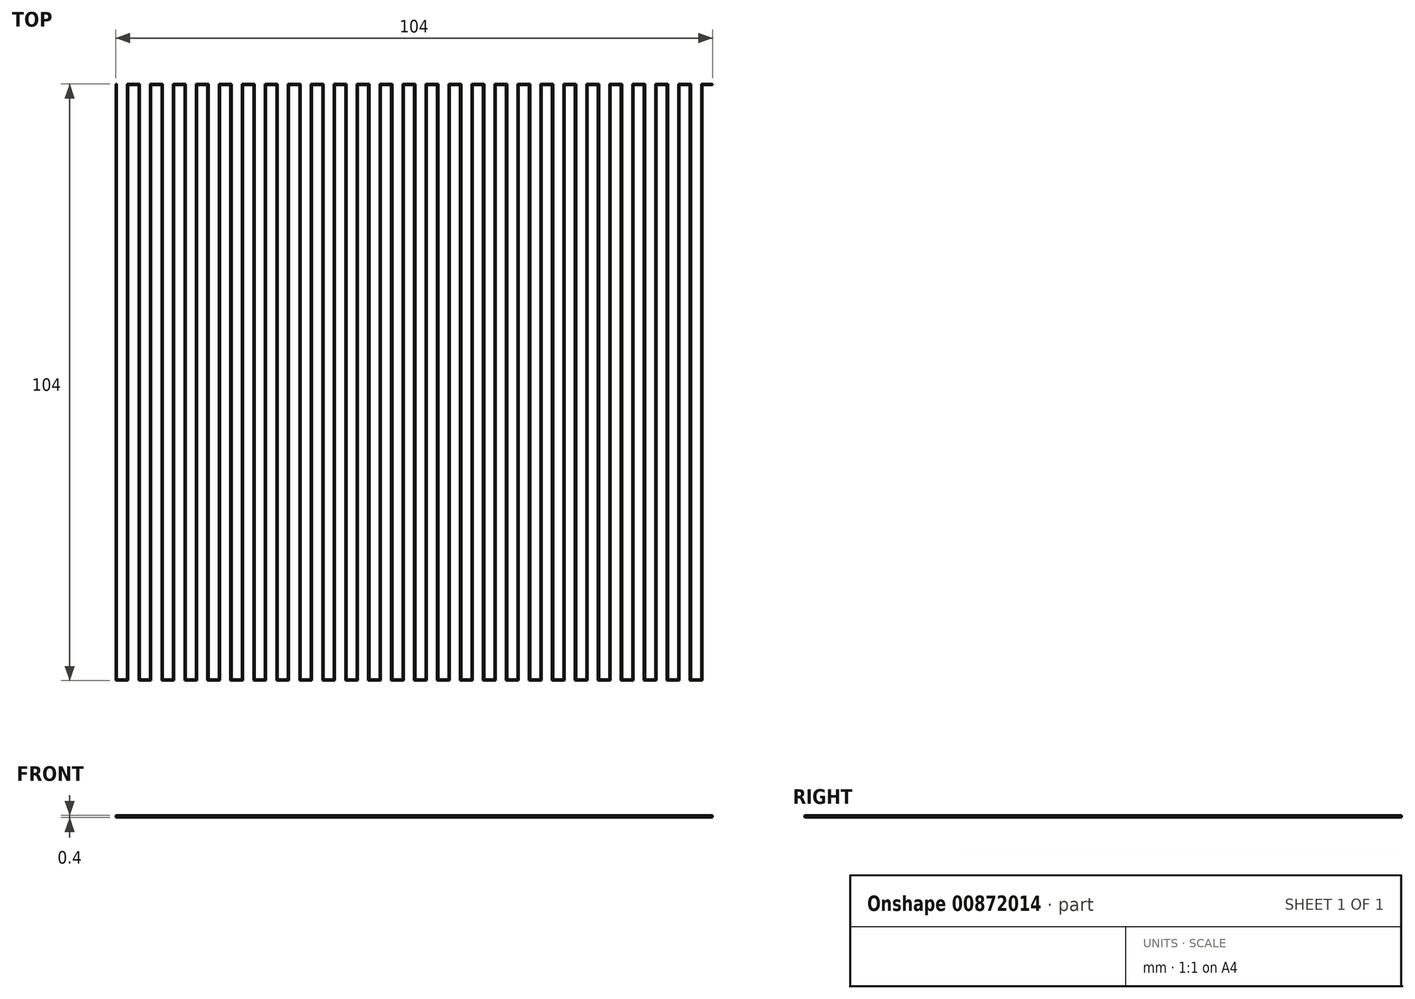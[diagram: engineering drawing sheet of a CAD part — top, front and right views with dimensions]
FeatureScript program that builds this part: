
annotation { "Feature Type Name" : "Feature", "Feature Type Description" : "" }
export const myFeature = defineFeature(function(context is Context, id is Id, definition is map)
    precondition{}
    {
        {
            var Q0;
            Q0=qCreatedBy(makeId("Top.planeOp"),FACE);
            var sketch = newSketch(context, id + "F0", { "sketchPlane" : qUnion([Q0])});
            skLineSegment(sketch, "E0.bottom", {"start": v(-50.6, 46.07) * mm, "end": v(-50.4, 46.07) * mm});
            skLineSegment(sketch, "E0.top", {"start": v(-50.6, -57.93) * mm, "end": v(-50.4, -57.93) * mm});
            skLineSegment(sketch, "E0.left", {"start": v(-50.6, 46.07) * mm, "end": v(-50.6, -57.93) * mm});
            skLineSegment(sketch, "E0.right", {"start": v(-50.4, 46.07) * mm, "end": v(-50.4, -57.93) * mm});
            skLineSegment(sketch, "E1.bottom", {"start": v(-50.6, -57.93) * mm, "end": v(-48.6, -57.93) * mm});
            skLineSegment(sketch, "E1.top", {"start": v(-50.6, -57.73) * mm, "end": v(-48.6, -57.73) * mm});
            skLineSegment(sketch, "E1.left", {"start": v(-50.6, -57.93) * mm, "end": v(-50.6, -57.73) * mm});
            skLineSegment(sketch, "E1.right", {"start": v(-48.6, -57.93) * mm, "end": v(-48.6, -57.73) * mm});
            skLineSegment(sketch, "E2.bottom", {"start": v(-48.6, -57.93) * mm, "end": v(-48.4, -57.93) * mm});
            skLineSegment(sketch, "E2.top", {"start": v(-48.6, 46.07) * mm, "end": v(-48.4, 46.07) * mm});
            skLineSegment(sketch, "E2.left", {"start": v(-48.6, -57.93) * mm, "end": v(-48.6, 46.07) * mm});
            skLineSegment(sketch, "E2.right", {"start": v(-48.4, -57.93) * mm, "end": v(-48.4, 46.07) * mm});
            skLineSegment(sketch, "E3.bottom", {"start": v(-48.6, 46.07) * mm, "end": v(-46.6, 46.07) * mm});
            skLineSegment(sketch, "E3.top", {"start": v(-48.6, 45.87) * mm, "end": v(-46.6, 45.87) * mm});
            skLineSegment(sketch, "E3.left", {"start": v(-48.6, 46.07) * mm, "end": v(-48.6, 45.87) * mm});
            skLineSegment(sketch, "E3.right", {"start": v(-46.6, 46.07) * mm, "end": v(-46.6, 45.87) * mm});
            skLineSegment(sketch, "E4.1.0.0", {"start": v(-46.4, 46.07) * mm, "end": v(-46.4, -57.93) * mm});
            skLineSegment(sketch, "E4.1.0.1", {"start": v(-46.6, 46.07) * mm, "end": v(-46.6, -57.93) * mm});
            skLineSegment(sketch, "E4.1.0.2", {"start": v(-44.4, -57.93) * mm, "end": v(-44.4, 46.07) * mm});
            skLineSegment(sketch, "E4.1.0.3", {"start": v(-44.6, -57.93) * mm, "end": v(-44.6, 46.07) * mm});
            skLineSegment(sketch, "E4.1.0.4", {"start": v(-44.6, 45.87) * mm, "end": v(-42.6, 45.87) * mm});
            skLineSegment(sketch, "E4.1.0.5", {"start": v(-46.6, 46.07) * mm, "end": v(-46.4, 46.07) * mm});
            skLineSegment(sketch, "E4.1.0.6", {"start": v(-44.6, 46.07) * mm, "end": v(-42.6, 46.07) * mm});
            skLineSegment(sketch, "E4.1.0.7", {"start": v(-42.6, 46.07) * mm, "end": v(-42.6, 45.87) * mm});
            skLineSegment(sketch, "E4.1.0.8", {"start": v(-46.6, -57.73) * mm, "end": v(-44.6, -57.73) * mm});
            skLineSegment(sketch, "E4.1.0.9", {"start": v(-46.6, -57.93) * mm, "end": v(-44.6, -57.93) * mm});
            skLineSegment(sketch, "E4.1.0.10", {"start": v(-46.6, -57.93) * mm, "end": v(-46.4, -57.93) * mm});
            skLineSegment(sketch, "E4.1.0.11", {"start": v(-46.6, -57.93) * mm, "end": v(-46.6, -57.73) * mm});
            skLineSegment(sketch, "E4.1.0.12", {"start": v(-44.6, -57.93) * mm, "end": v(-44.6, -57.73) * mm});
            skLineSegment(sketch, "E4.1.0.13", {"start": v(-44.6, -57.93) * mm, "end": v(-44.4, -57.93) * mm});
            skLineSegment(sketch, "E4.1.0.14", {"start": v(-44.6, 46.07) * mm, "end": v(-44.4, 46.07) * mm});
            skLineSegment(sketch, "E4.1.0.15", {"start": v(-44.6, 46.07) * mm, "end": v(-44.6, 45.87) * mm});
            skLineSegment(sketch, "E4.2.0.0", {"start": v(-42.4, 46.07) * mm, "end": v(-42.4, -57.93) * mm});
            skLineSegment(sketch, "E4.2.0.1", {"start": v(-42.6, 46.07) * mm, "end": v(-42.6, -57.93) * mm});
            skLineSegment(sketch, "E4.2.0.2", {"start": v(-40.4, -57.93) * mm, "end": v(-40.4, 46.07) * mm});
            skLineSegment(sketch, "E4.2.0.3", {"start": v(-40.6, -57.93) * mm, "end": v(-40.6, 46.07) * mm});
            skLineSegment(sketch, "E4.2.0.4", {"start": v(-40.6, 45.87) * mm, "end": v(-38.6, 45.87) * mm});
            skLineSegment(sketch, "E4.2.0.5", {"start": v(-42.6, 46.07) * mm, "end": v(-42.4, 46.07) * mm});
            skLineSegment(sketch, "E4.2.0.6", {"start": v(-40.6, 46.07) * mm, "end": v(-38.6, 46.07) * mm});
            skLineSegment(sketch, "E4.2.0.7", {"start": v(-38.6, 46.07) * mm, "end": v(-38.6, 45.87) * mm});
            skLineSegment(sketch, "E4.2.0.8", {"start": v(-42.6, -57.73) * mm, "end": v(-40.6, -57.73) * mm});
            skLineSegment(sketch, "E4.2.0.9", {"start": v(-42.6, -57.93) * mm, "end": v(-40.6, -57.93) * mm});
            skLineSegment(sketch, "E4.2.0.10", {"start": v(-42.6, -57.93) * mm, "end": v(-42.4, -57.93) * mm});
            skLineSegment(sketch, "E4.2.0.11", {"start": v(-42.6, -57.93) * mm, "end": v(-42.6, -57.73) * mm});
            skLineSegment(sketch, "E4.2.0.12", {"start": v(-40.6, -57.93) * mm, "end": v(-40.6, -57.73) * mm});
            skLineSegment(sketch, "E4.2.0.13", {"start": v(-40.6, -57.93) * mm, "end": v(-40.4, -57.93) * mm});
            skLineSegment(sketch, "E4.2.0.14", {"start": v(-40.6, 46.07) * mm, "end": v(-40.4, 46.07) * mm});
            skLineSegment(sketch, "E4.2.0.15", {"start": v(-40.6, 46.07) * mm, "end": v(-40.6, 45.87) * mm});
            skLineSegment(sketch, "E4.3.0.0", {"start": v(-38.4, 46.07) * mm, "end": v(-38.4, -57.93) * mm});
            skLineSegment(sketch, "E4.3.0.1", {"start": v(-38.6, 46.07) * mm, "end": v(-38.6, -57.93) * mm});
            skLineSegment(sketch, "E4.3.0.2", {"start": v(-36.4, -57.93) * mm, "end": v(-36.4, 46.07) * mm});
            skLineSegment(sketch, "E4.3.0.3", {"start": v(-36.6, -57.93) * mm, "end": v(-36.6, 46.07) * mm});
            skLineSegment(sketch, "E4.3.0.4", {"start": v(-36.6, 45.87) * mm, "end": v(-34.6, 45.87) * mm});
            skLineSegment(sketch, "E4.3.0.5", {"start": v(-38.6, 46.07) * mm, "end": v(-38.4, 46.07) * mm});
            skLineSegment(sketch, "E4.3.0.6", {"start": v(-36.6, 46.07) * mm, "end": v(-34.6, 46.07) * mm});
            skLineSegment(sketch, "E4.3.0.7", {"start": v(-34.6, 46.07) * mm, "end": v(-34.6, 45.87) * mm});
            skLineSegment(sketch, "E4.3.0.8", {"start": v(-38.6, -57.73) * mm, "end": v(-36.6, -57.73) * mm});
            skLineSegment(sketch, "E4.3.0.9", {"start": v(-38.6, -57.93) * mm, "end": v(-36.6, -57.93) * mm});
            skLineSegment(sketch, "E4.3.0.10", {"start": v(-38.6, -57.93) * mm, "end": v(-38.4, -57.93) * mm});
            skLineSegment(sketch, "E4.3.0.11", {"start": v(-38.6, -57.93) * mm, "end": v(-38.6, -57.73) * mm});
            skLineSegment(sketch, "E4.3.0.12", {"start": v(-36.6, -57.93) * mm, "end": v(-36.6, -57.73) * mm});
            skLineSegment(sketch, "E4.3.0.13", {"start": v(-36.6, -57.93) * mm, "end": v(-36.4, -57.93) * mm});
            skLineSegment(sketch, "E4.3.0.14", {"start": v(-36.6, 46.07) * mm, "end": v(-36.4, 46.07) * mm});
            skLineSegment(sketch, "E4.3.0.15", {"start": v(-36.6, 46.07) * mm, "end": v(-36.6, 45.87) * mm});
            skLineSegment(sketch, "E4.4.0.0", {"start": v(-34.4, 46.07) * mm, "end": v(-34.4, -57.93) * mm});
            skLineSegment(sketch, "E4.4.0.1", {"start": v(-34.6, 46.07) * mm, "end": v(-34.6, -57.93) * mm});
            skLineSegment(sketch, "E4.4.0.2", {"start": v(-32.4, -57.93) * mm, "end": v(-32.4, 46.07) * mm});
            skLineSegment(sketch, "E4.4.0.3", {"start": v(-32.6, -57.93) * mm, "end": v(-32.6, 46.07) * mm});
            skLineSegment(sketch, "E4.4.0.4", {"start": v(-32.6, 45.87) * mm, "end": v(-30.6, 45.87) * mm});
            skLineSegment(sketch, "E4.4.0.5", {"start": v(-34.6, 46.07) * mm, "end": v(-34.4, 46.07) * mm});
            skLineSegment(sketch, "E4.4.0.6", {"start": v(-32.6, 46.07) * mm, "end": v(-30.6, 46.07) * mm});
            skLineSegment(sketch, "E4.4.0.7", {"start": v(-30.6, 46.07) * mm, "end": v(-30.6, 45.87) * mm});
            skLineSegment(sketch, "E4.4.0.8", {"start": v(-34.6, -57.73) * mm, "end": v(-32.6, -57.73) * mm});
            skLineSegment(sketch, "E4.4.0.9", {"start": v(-34.6, -57.93) * mm, "end": v(-32.6, -57.93) * mm});
            skLineSegment(sketch, "E4.4.0.10", {"start": v(-34.6, -57.93) * mm, "end": v(-34.4, -57.93) * mm});
            skLineSegment(sketch, "E4.4.0.11", {"start": v(-34.6, -57.93) * mm, "end": v(-34.6, -57.73) * mm});
            skLineSegment(sketch, "E4.4.0.12", {"start": v(-32.6, -57.93) * mm, "end": v(-32.6, -57.73) * mm});
            skLineSegment(sketch, "E4.4.0.13", {"start": v(-32.6, -57.93) * mm, "end": v(-32.4, -57.93) * mm});
            skLineSegment(sketch, "E4.4.0.14", {"start": v(-32.6, 46.07) * mm, "end": v(-32.4, 46.07) * mm});
            skLineSegment(sketch, "E4.4.0.15", {"start": v(-32.6, 46.07) * mm, "end": v(-32.6, 45.87) * mm});
            skLineSegment(sketch, "E4.5.0.0", {"start": v(-30.4, 46.07) * mm, "end": v(-30.4, -57.93) * mm});
            skLineSegment(sketch, "E4.5.0.1", {"start": v(-30.6, 46.07) * mm, "end": v(-30.6, -57.93) * mm});
            skLineSegment(sketch, "E4.5.0.2", {"start": v(-28.4, -57.93) * mm, "end": v(-28.4, 46.07) * mm});
            skLineSegment(sketch, "E4.5.0.3", {"start": v(-28.6, -57.93) * mm, "end": v(-28.6, 46.07) * mm});
            skLineSegment(sketch, "E4.5.0.4", {"start": v(-28.6, 45.87) * mm, "end": v(-26.6, 45.87) * mm});
            skLineSegment(sketch, "E4.5.0.5", {"start": v(-30.6, 46.07) * mm, "end": v(-30.4, 46.07) * mm});
            skLineSegment(sketch, "E4.5.0.6", {"start": v(-28.6, 46.07) * mm, "end": v(-26.6, 46.07) * mm});
            skLineSegment(sketch, "E4.5.0.7", {"start": v(-26.6, 46.07) * mm, "end": v(-26.6, 45.87) * mm});
            skLineSegment(sketch, "E4.5.0.8", {"start": v(-30.6, -57.73) * mm, "end": v(-28.6, -57.73) * mm});
            skLineSegment(sketch, "E4.5.0.9", {"start": v(-30.6, -57.93) * mm, "end": v(-28.6, -57.93) * mm});
            skLineSegment(sketch, "E4.5.0.10", {"start": v(-30.6, -57.93) * mm, "end": v(-30.4, -57.93) * mm});
            skLineSegment(sketch, "E4.5.0.11", {"start": v(-30.6, -57.93) * mm, "end": v(-30.6, -57.73) * mm});
            skLineSegment(sketch, "E4.5.0.12", {"start": v(-28.6, -57.93) * mm, "end": v(-28.6, -57.73) * mm});
            skLineSegment(sketch, "E4.5.0.13", {"start": v(-28.6, -57.93) * mm, "end": v(-28.4, -57.93) * mm});
            skLineSegment(sketch, "E4.5.0.14", {"start": v(-28.6, 46.07) * mm, "end": v(-28.4, 46.07) * mm});
            skLineSegment(sketch, "E4.5.0.15", {"start": v(-28.6, 46.07) * mm, "end": v(-28.6, 45.87) * mm});
            skLineSegment(sketch, "E4.6.0.0", {"start": v(-26.4, 46.07) * mm, "end": v(-26.4, -57.93) * mm});
            skLineSegment(sketch, "E4.6.0.1", {"start": v(-26.6, 46.07) * mm, "end": v(-26.6, -57.93) * mm});
            skLineSegment(sketch, "E4.6.0.2", {"start": v(-24.4, -57.93) * mm, "end": v(-24.4, 46.07) * mm});
            skLineSegment(sketch, "E4.6.0.3", {"start": v(-24.6, -57.93) * mm, "end": v(-24.6, 46.07) * mm});
            skLineSegment(sketch, "E4.6.0.4", {"start": v(-24.6, 45.87) * mm, "end": v(-22.6, 45.87) * mm});
            skLineSegment(sketch, "E4.6.0.5", {"start": v(-26.6, 46.07) * mm, "end": v(-26.4, 46.07) * mm});
            skLineSegment(sketch, "E4.6.0.6", {"start": v(-24.6, 46.07) * mm, "end": v(-22.6, 46.07) * mm});
            skLineSegment(sketch, "E4.6.0.7", {"start": v(-22.6, 46.07) * mm, "end": v(-22.6, 45.87) * mm});
            skLineSegment(sketch, "E4.6.0.8", {"start": v(-26.6, -57.73) * mm, "end": v(-24.6, -57.73) * mm});
            skLineSegment(sketch, "E4.6.0.9", {"start": v(-26.6, -57.93) * mm, "end": v(-24.6, -57.93) * mm});
            skLineSegment(sketch, "E4.6.0.10", {"start": v(-26.6, -57.93) * mm, "end": v(-26.4, -57.93) * mm});
            skLineSegment(sketch, "E4.6.0.11", {"start": v(-26.6, -57.93) * mm, "end": v(-26.6, -57.73) * mm});
            skLineSegment(sketch, "E4.6.0.12", {"start": v(-24.6, -57.93) * mm, "end": v(-24.6, -57.73) * mm});
            skLineSegment(sketch, "E4.6.0.13", {"start": v(-24.6, -57.93) * mm, "end": v(-24.4, -57.93) * mm});
            skLineSegment(sketch, "E4.6.0.14", {"start": v(-24.6, 46.07) * mm, "end": v(-24.4, 46.07) * mm});
            skLineSegment(sketch, "E4.6.0.15", {"start": v(-24.6, 46.07) * mm, "end": v(-24.6, 45.87) * mm});
            skLineSegment(sketch, "E4.7.0.0", {"start": v(-22.4, 46.07) * mm, "end": v(-22.4, -57.93) * mm});
            skLineSegment(sketch, "E4.7.0.1", {"start": v(-22.6, 46.07) * mm, "end": v(-22.6, -57.93) * mm});
            skLineSegment(sketch, "E4.7.0.2", {"start": v(-20.4, -57.93) * mm, "end": v(-20.4, 46.07) * mm});
            skLineSegment(sketch, "E4.7.0.3", {"start": v(-20.6, -57.93) * mm, "end": v(-20.6, 46.07) * mm});
            skLineSegment(sketch, "E4.7.0.4", {"start": v(-20.6, 45.87) * mm, "end": v(-18.6, 45.87) * mm});
            skLineSegment(sketch, "E4.7.0.5", {"start": v(-22.6, 46.07) * mm, "end": v(-22.4, 46.07) * mm});
            skLineSegment(sketch, "E4.7.0.6", {"start": v(-20.6, 46.07) * mm, "end": v(-18.6, 46.07) * mm});
            skLineSegment(sketch, "E4.7.0.7", {"start": v(-18.6, 46.07) * mm, "end": v(-18.6, 45.87) * mm});
            skLineSegment(sketch, "E4.7.0.8", {"start": v(-22.6, -57.73) * mm, "end": v(-20.6, -57.73) * mm});
            skLineSegment(sketch, "E4.7.0.9", {"start": v(-22.6, -57.93) * mm, "end": v(-20.6, -57.93) * mm});
            skLineSegment(sketch, "E4.7.0.10", {"start": v(-22.6, -57.93) * mm, "end": v(-22.4, -57.93) * mm});
            skLineSegment(sketch, "E4.7.0.11", {"start": v(-22.6, -57.93) * mm, "end": v(-22.6, -57.73) * mm});
            skLineSegment(sketch, "E4.7.0.12", {"start": v(-20.6, -57.93) * mm, "end": v(-20.6, -57.73) * mm});
            skLineSegment(sketch, "E4.7.0.13", {"start": v(-20.6, -57.93) * mm, "end": v(-20.4, -57.93) * mm});
            skLineSegment(sketch, "E4.7.0.14", {"start": v(-20.6, 46.07) * mm, "end": v(-20.4, 46.07) * mm});
            skLineSegment(sketch, "E4.7.0.15", {"start": v(-20.6, 46.07) * mm, "end": v(-20.6, 45.87) * mm});
            skLineSegment(sketch, "E4.8.0.0", {"start": v(-18.4, 46.07) * mm, "end": v(-18.4, -57.93) * mm});
            skLineSegment(sketch, "E4.8.0.1", {"start": v(-18.6, 46.07) * mm, "end": v(-18.6, -57.93) * mm});
            skLineSegment(sketch, "E4.8.0.2", {"start": v(-16.4, -57.93) * mm, "end": v(-16.4, 46.07) * mm});
            skLineSegment(sketch, "E4.8.0.3", {"start": v(-16.6, -57.93) * mm, "end": v(-16.6, 46.07) * mm});
            skLineSegment(sketch, "E4.8.0.4", {"start": v(-16.6, 45.87) * mm, "end": v(-14.6, 45.87) * mm});
            skLineSegment(sketch, "E4.8.0.5", {"start": v(-18.6, 46.07) * mm, "end": v(-18.4, 46.07) * mm});
            skLineSegment(sketch, "E4.8.0.6", {"start": v(-16.6, 46.07) * mm, "end": v(-14.6, 46.07) * mm});
            skLineSegment(sketch, "E4.8.0.7", {"start": v(-14.6, 46.07) * mm, "end": v(-14.6, 45.87) * mm});
            skLineSegment(sketch, "E4.8.0.8", {"start": v(-18.6, -57.73) * mm, "end": v(-16.6, -57.73) * mm});
            skLineSegment(sketch, "E4.8.0.9", {"start": v(-18.6, -57.93) * mm, "end": v(-16.6, -57.93) * mm});
            skLineSegment(sketch, "E4.8.0.10", {"start": v(-18.6, -57.93) * mm, "end": v(-18.4, -57.93) * mm});
            skLineSegment(sketch, "E4.8.0.11", {"start": v(-18.6, -57.93) * mm, "end": v(-18.6, -57.73) * mm});
            skLineSegment(sketch, "E4.8.0.12", {"start": v(-16.6, -57.93) * mm, "end": v(-16.6, -57.73) * mm});
            skLineSegment(sketch, "E4.8.0.13", {"start": v(-16.6, -57.93) * mm, "end": v(-16.4, -57.93) * mm});
            skLineSegment(sketch, "E4.8.0.14", {"start": v(-16.6, 46.07) * mm, "end": v(-16.4, 46.07) * mm});
            skLineSegment(sketch, "E4.8.0.15", {"start": v(-16.6, 46.07) * mm, "end": v(-16.6, 45.87) * mm});
            skLineSegment(sketch, "E4.9.0.0", {"start": v(-14.4, 46.07) * mm, "end": v(-14.4, -57.93) * mm});
            skLineSegment(sketch, "E4.9.0.1", {"start": v(-14.6, 46.07) * mm, "end": v(-14.6, -57.93) * mm});
            skLineSegment(sketch, "E4.9.0.2", {"start": v(-12.4, -57.93) * mm, "end": v(-12.4, 46.07) * mm});
            skLineSegment(sketch, "E4.9.0.3", {"start": v(-12.6, -57.93) * mm, "end": v(-12.6, 46.07) * mm});
            skLineSegment(sketch, "E4.9.0.4", {"start": v(-12.6, 45.87) * mm, "end": v(-10.6, 45.87) * mm});
            skLineSegment(sketch, "E4.9.0.5", {"start": v(-14.6, 46.07) * mm, "end": v(-14.4, 46.07) * mm});
            skLineSegment(sketch, "E4.9.0.6", {"start": v(-12.6, 46.07) * mm, "end": v(-10.6, 46.07) * mm});
            skLineSegment(sketch, "E4.9.0.7", {"start": v(-10.6, 46.07) * mm, "end": v(-10.6, 45.87) * mm});
            skLineSegment(sketch, "E4.9.0.8", {"start": v(-14.6, -57.73) * mm, "end": v(-12.6, -57.73) * mm});
            skLineSegment(sketch, "E4.9.0.9", {"start": v(-14.6, -57.93) * mm, "end": v(-12.6, -57.93) * mm});
            skLineSegment(sketch, "E4.9.0.10", {"start": v(-14.6, -57.93) * mm, "end": v(-14.4, -57.93) * mm});
            skLineSegment(sketch, "E4.9.0.11", {"start": v(-14.6, -57.93) * mm, "end": v(-14.6, -57.73) * mm});
            skLineSegment(sketch, "E4.9.0.12", {"start": v(-12.6, -57.93) * mm, "end": v(-12.6, -57.73) * mm});
            skLineSegment(sketch, "E4.9.0.13", {"start": v(-12.6, -57.93) * mm, "end": v(-12.4, -57.93) * mm});
            skLineSegment(sketch, "E4.9.0.14", {"start": v(-12.6, 46.07) * mm, "end": v(-12.4, 46.07) * mm});
            skLineSegment(sketch, "E4.9.0.15", {"start": v(-12.6, 46.07) * mm, "end": v(-12.6, 45.87) * mm});
            skLineSegment(sketch, "E4.10.0.0", {"start": v(-10.4, 46.07) * mm, "end": v(-10.4, -57.93) * mm});
            skLineSegment(sketch, "E4.10.0.1", {"start": v(-10.6, 46.07) * mm, "end": v(-10.6, -57.93) * mm});
            skLineSegment(sketch, "E4.10.0.2", {"start": v(-8.4, -57.93) * mm, "end": v(-8.4, 46.07) * mm});
            skLineSegment(sketch, "E4.10.0.3", {"start": v(-8.6, -57.93) * mm, "end": v(-8.6, 46.07) * mm});
            skLineSegment(sketch, "E4.10.0.4", {"start": v(-8.6, 45.87) * mm, "end": v(-6.6, 45.87) * mm});
            skLineSegment(sketch, "E4.10.0.5", {"start": v(-10.6, 46.07) * mm, "end": v(-10.4, 46.07) * mm});
            skLineSegment(sketch, "E4.10.0.6", {"start": v(-8.6, 46.07) * mm, "end": v(-6.6, 46.07) * mm});
            skLineSegment(sketch, "E4.10.0.7", {"start": v(-6.6, 46.07) * mm, "end": v(-6.6, 45.87) * mm});
            skLineSegment(sketch, "E4.10.0.8", {"start": v(-10.6, -57.73) * mm, "end": v(-8.6, -57.73) * mm});
            skLineSegment(sketch, "E4.10.0.9", {"start": v(-10.6, -57.93) * mm, "end": v(-8.6, -57.93) * mm});
            skLineSegment(sketch, "E4.10.0.10", {"start": v(-10.6, -57.93) * mm, "end": v(-10.4, -57.93) * mm});
            skLineSegment(sketch, "E4.10.0.11", {"start": v(-10.6, -57.93) * mm, "end": v(-10.6, -57.73) * mm});
            skLineSegment(sketch, "E4.10.0.12", {"start": v(-8.6, -57.93) * mm, "end": v(-8.6, -57.73) * mm});
            skLineSegment(sketch, "E4.10.0.13", {"start": v(-8.6, -57.93) * mm, "end": v(-8.4, -57.93) * mm});
            skLineSegment(sketch, "E4.10.0.14", {"start": v(-8.6, 46.07) * mm, "end": v(-8.4, 46.07) * mm});
            skLineSegment(sketch, "E4.10.0.15", {"start": v(-8.6, 46.07) * mm, "end": v(-8.6, 45.87) * mm});
            skLineSegment(sketch, "E4.11.0.0", {"start": v(-6.4, 46.07) * mm, "end": v(-6.4, -57.93) * mm});
            skLineSegment(sketch, "E4.11.0.1", {"start": v(-6.6, 46.07) * mm, "end": v(-6.6, -57.93) * mm});
            skLineSegment(sketch, "E4.11.0.2", {"start": v(-4.4, -57.93) * mm, "end": v(-4.4, 46.07) * mm});
            skLineSegment(sketch, "E4.11.0.3", {"start": v(-4.6, -57.93) * mm, "end": v(-4.6, 46.07) * mm});
            skLineSegment(sketch, "E4.11.0.4", {"start": v(-4.6, 45.87) * mm, "end": v(-2.6, 45.87) * mm});
            skLineSegment(sketch, "E4.11.0.5", {"start": v(-6.6, 46.07) * mm, "end": v(-6.4, 46.07) * mm});
            skLineSegment(sketch, "E4.11.0.6", {"start": v(-4.6, 46.07) * mm, "end": v(-2.6, 46.07) * mm});
            skLineSegment(sketch, "E4.11.0.7", {"start": v(-2.6, 46.07) * mm, "end": v(-2.6, 45.87) * mm});
            skLineSegment(sketch, "E4.11.0.8", {"start": v(-6.6, -57.73) * mm, "end": v(-4.6, -57.73) * mm});
            skLineSegment(sketch, "E4.11.0.9", {"start": v(-6.6, -57.93) * mm, "end": v(-4.6, -57.93) * mm});
            skLineSegment(sketch, "E4.11.0.10", {"start": v(-6.6, -57.93) * mm, "end": v(-6.4, -57.93) * mm});
            skLineSegment(sketch, "E4.11.0.11", {"start": v(-6.6, -57.93) * mm, "end": v(-6.6, -57.73) * mm});
            skLineSegment(sketch, "E4.11.0.12", {"start": v(-4.6, -57.93) * mm, "end": v(-4.6, -57.73) * mm});
            skLineSegment(sketch, "E4.11.0.13", {"start": v(-4.6, -57.93) * mm, "end": v(-4.4, -57.93) * mm});
            skLineSegment(sketch, "E4.11.0.14", {"start": v(-4.6, 46.07) * mm, "end": v(-4.4, 46.07) * mm});
            skLineSegment(sketch, "E4.11.0.15", {"start": v(-4.6, 46.07) * mm, "end": v(-4.6, 45.87) * mm});
            skLineSegment(sketch, "E4.12.0.0", {"start": v(-2.4, 46.07) * mm, "end": v(-2.4, -57.93) * mm});
            skLineSegment(sketch, "E4.12.0.1", {"start": v(-2.6, 46.07) * mm, "end": v(-2.6, -57.93) * mm});
            skLineSegment(sketch, "E4.12.0.2", {"start": v(-0.4, -57.93) * mm, "end": v(-0.4, 46.07) * mm});
            skLineSegment(sketch, "E4.12.0.3", {"start": v(-0.6, -57.93) * mm, "end": v(-0.6, 46.07) * mm});
            skLineSegment(sketch, "E4.12.0.4", {"start": v(-0.6, 45.87) * mm, "end": v(1.4, 45.87) * mm});
            skLineSegment(sketch, "E4.12.0.5", {"start": v(-2.6, 46.07) * mm, "end": v(-2.4, 46.07) * mm});
            skLineSegment(sketch, "E4.12.0.6", {"start": v(-0.6, 46.07) * mm, "end": v(1.4, 46.07) * mm});
            skLineSegment(sketch, "E4.12.0.7", {"start": v(1.4, 46.07) * mm, "end": v(1.4, 45.87) * mm});
            skLineSegment(sketch, "E4.12.0.8", {"start": v(-2.6, -57.73) * mm, "end": v(-0.6, -57.73) * mm});
            skLineSegment(sketch, "E4.12.0.9", {"start": v(-2.6, -57.93) * mm, "end": v(-0.6, -57.93) * mm});
            skLineSegment(sketch, "E4.12.0.10", {"start": v(-2.6, -57.93) * mm, "end": v(-2.4, -57.93) * mm});
            skLineSegment(sketch, "E4.12.0.11", {"start": v(-2.6, -57.93) * mm, "end": v(-2.6, -57.73) * mm});
            skLineSegment(sketch, "E4.12.0.12", {"start": v(-0.6, -57.93) * mm, "end": v(-0.6, -57.73) * mm});
            skLineSegment(sketch, "E4.12.0.13", {"start": v(-0.6, -57.93) * mm, "end": v(-0.4, -57.93) * mm});
            skLineSegment(sketch, "E4.12.0.14", {"start": v(-0.6, 46.07) * mm, "end": v(-0.4, 46.07) * mm});
            skLineSegment(sketch, "E4.12.0.15", {"start": v(-0.6, 46.07) * mm, "end": v(-0.6, 45.87) * mm});
            skLineSegment(sketch, "E4.13.0.0", {"start": v(1.6, 46.07) * mm, "end": v(1.6, -57.93) * mm});
            skLineSegment(sketch, "E4.13.0.1", {"start": v(1.4, 46.07) * mm, "end": v(1.4, -57.93) * mm});
            skLineSegment(sketch, "E4.13.0.2", {"start": v(3.6, -57.93) * mm, "end": v(3.6, 46.07) * mm});
            skLineSegment(sketch, "E4.13.0.3", {"start": v(3.4, -57.93) * mm, "end": v(3.4, 46.07) * mm});
            skLineSegment(sketch, "E4.13.0.4", {"start": v(3.4, 45.87) * mm, "end": v(5.4, 45.87) * mm});
            skLineSegment(sketch, "E4.13.0.5", {"start": v(1.4, 46.07) * mm, "end": v(1.6, 46.07) * mm});
            skLineSegment(sketch, "E4.13.0.6", {"start": v(3.4, 46.07) * mm, "end": v(5.4, 46.07) * mm});
            skLineSegment(sketch, "E4.13.0.7", {"start": v(5.4, 46.07) * mm, "end": v(5.4, 45.87) * mm});
            skLineSegment(sketch, "E4.13.0.8", {"start": v(1.4, -57.73) * mm, "end": v(3.4, -57.73) * mm});
            skLineSegment(sketch, "E4.13.0.9", {"start": v(1.4, -57.93) * mm, "end": v(3.4, -57.93) * mm});
            skLineSegment(sketch, "E4.13.0.10", {"start": v(1.4, -57.93) * mm, "end": v(1.6, -57.93) * mm});
            skLineSegment(sketch, "E4.13.0.11", {"start": v(1.4, -57.93) * mm, "end": v(1.4, -57.73) * mm});
            skLineSegment(sketch, "E4.13.0.12", {"start": v(3.4, -57.93) * mm, "end": v(3.4, -57.73) * mm});
            skLineSegment(sketch, "E4.13.0.13", {"start": v(3.4, -57.93) * mm, "end": v(3.6, -57.93) * mm});
            skLineSegment(sketch, "E4.13.0.14", {"start": v(3.4, 46.07) * mm, "end": v(3.6, 46.07) * mm});
            skLineSegment(sketch, "E4.13.0.15", {"start": v(3.4, 46.07) * mm, "end": v(3.4, 45.87) * mm});
            skLineSegment(sketch, "E4.14.0.0", {"start": v(5.6, 46.07) * mm, "end": v(5.6, -57.93) * mm});
            skLineSegment(sketch, "E4.14.0.1", {"start": v(5.4, 46.07) * mm, "end": v(5.4, -57.93) * mm});
            skLineSegment(sketch, "E4.14.0.2", {"start": v(7.6, -57.93) * mm, "end": v(7.6, 46.07) * mm});
            skLineSegment(sketch, "E4.14.0.3", {"start": v(7.4, -57.93) * mm, "end": v(7.4, 46.07) * mm});
            skLineSegment(sketch, "E4.14.0.4", {"start": v(7.4, 45.87) * mm, "end": v(9.4, 45.87) * mm});
            skLineSegment(sketch, "E4.14.0.5", {"start": v(5.4, 46.07) * mm, "end": v(5.6, 46.07) * mm});
            skLineSegment(sketch, "E4.14.0.6", {"start": v(7.4, 46.07) * mm, "end": v(9.4, 46.07) * mm});
            skLineSegment(sketch, "E4.14.0.7", {"start": v(9.4, 46.07) * mm, "end": v(9.4, 45.87) * mm});
            skLineSegment(sketch, "E4.14.0.8", {"start": v(5.4, -57.73) * mm, "end": v(7.4, -57.73) * mm});
            skLineSegment(sketch, "E4.14.0.9", {"start": v(5.4, -57.93) * mm, "end": v(7.4, -57.93) * mm});
            skLineSegment(sketch, "E4.14.0.10", {"start": v(5.4, -57.93) * mm, "end": v(5.6, -57.93) * mm});
            skLineSegment(sketch, "E4.14.0.11", {"start": v(5.4, -57.93) * mm, "end": v(5.4, -57.73) * mm});
            skLineSegment(sketch, "E4.14.0.12", {"start": v(7.4, -57.93) * mm, "end": v(7.4, -57.73) * mm});
            skLineSegment(sketch, "E4.14.0.13", {"start": v(7.4, -57.93) * mm, "end": v(7.6, -57.93) * mm});
            skLineSegment(sketch, "E4.14.0.14", {"start": v(7.4, 46.07) * mm, "end": v(7.6, 46.07) * mm});
            skLineSegment(sketch, "E4.14.0.15", {"start": v(7.4, 46.07) * mm, "end": v(7.4, 45.87) * mm});
            skLineSegment(sketch, "E4.15.0.0", {"start": v(9.6, 46.07) * mm, "end": v(9.6, -57.93) * mm});
            skLineSegment(sketch, "E4.15.0.1", {"start": v(9.4, 46.07) * mm, "end": v(9.4, -57.93) * mm});
            skLineSegment(sketch, "E4.15.0.2", {"start": v(11.6, -57.93) * mm, "end": v(11.6, 46.07) * mm});
            skLineSegment(sketch, "E4.15.0.3", {"start": v(11.4, -57.93) * mm, "end": v(11.4, 46.07) * mm});
            skLineSegment(sketch, "E4.15.0.4", {"start": v(11.4, 45.87) * mm, "end": v(13.4, 45.87) * mm});
            skLineSegment(sketch, "E4.15.0.5", {"start": v(9.4, 46.07) * mm, "end": v(9.6, 46.07) * mm});
            skLineSegment(sketch, "E4.15.0.6", {"start": v(11.4, 46.07) * mm, "end": v(13.4, 46.07) * mm});
            skLineSegment(sketch, "E4.15.0.7", {"start": v(13.4, 46.07) * mm, "end": v(13.4, 45.87) * mm});
            skLineSegment(sketch, "E4.15.0.8", {"start": v(9.4, -57.73) * mm, "end": v(11.4, -57.73) * mm});
            skLineSegment(sketch, "E4.15.0.9", {"start": v(9.4, -57.93) * mm, "end": v(11.4, -57.93) * mm});
            skLineSegment(sketch, "E4.15.0.10", {"start": v(9.4, -57.93) * mm, "end": v(9.6, -57.93) * mm});
            skLineSegment(sketch, "E4.15.0.11", {"start": v(9.4, -57.93) * mm, "end": v(9.4, -57.73) * mm});
            skLineSegment(sketch, "E4.15.0.12", {"start": v(11.4, -57.93) * mm, "end": v(11.4, -57.73) * mm});
            skLineSegment(sketch, "E4.15.0.13", {"start": v(11.4, -57.93) * mm, "end": v(11.6, -57.93) * mm});
            skLineSegment(sketch, "E4.15.0.14", {"start": v(11.4, 46.07) * mm, "end": v(11.6, 46.07) * mm});
            skLineSegment(sketch, "E4.15.0.15", {"start": v(11.4, 46.07) * mm, "end": v(11.4, 45.87) * mm});
            skLineSegment(sketch, "E4.16.0.0", {"start": v(13.6, 46.07) * mm, "end": v(13.6, -57.93) * mm});
            skLineSegment(sketch, "E4.16.0.1", {"start": v(13.4, 46.07) * mm, "end": v(13.4, -57.93) * mm});
            skLineSegment(sketch, "E4.16.0.2", {"start": v(15.6, -57.93) * mm, "end": v(15.6, 46.07) * mm});
            skLineSegment(sketch, "E4.16.0.3", {"start": v(15.4, -57.93) * mm, "end": v(15.4, 46.07) * mm});
            skLineSegment(sketch, "E4.16.0.4", {"start": v(15.4, 45.87) * mm, "end": v(17.4, 45.87) * mm});
            skLineSegment(sketch, "E4.16.0.5", {"start": v(13.4, 46.07) * mm, "end": v(13.6, 46.07) * mm});
            skLineSegment(sketch, "E4.16.0.6", {"start": v(15.4, 46.07) * mm, "end": v(17.4, 46.07) * mm});
            skLineSegment(sketch, "E4.16.0.7", {"start": v(17.4, 46.07) * mm, "end": v(17.4, 45.87) * mm});
            skLineSegment(sketch, "E4.16.0.8", {"start": v(13.4, -57.73) * mm, "end": v(15.4, -57.73) * mm});
            skLineSegment(sketch, "E4.16.0.9", {"start": v(13.4, -57.93) * mm, "end": v(15.4, -57.93) * mm});
            skLineSegment(sketch, "E4.16.0.10", {"start": v(13.4, -57.93) * mm, "end": v(13.6, -57.93) * mm});
            skLineSegment(sketch, "E4.16.0.11", {"start": v(13.4, -57.93) * mm, "end": v(13.4, -57.73) * mm});
            skLineSegment(sketch, "E4.16.0.12", {"start": v(15.4, -57.93) * mm, "end": v(15.4, -57.73) * mm});
            skLineSegment(sketch, "E4.16.0.13", {"start": v(15.4, -57.93) * mm, "end": v(15.6, -57.93) * mm});
            skLineSegment(sketch, "E4.16.0.14", {"start": v(15.4, 46.07) * mm, "end": v(15.6, 46.07) * mm});
            skLineSegment(sketch, "E4.16.0.15", {"start": v(15.4, 46.07) * mm, "end": v(15.4, 45.87) * mm});
            skLineSegment(sketch, "E4.17.0.0", {"start": v(17.6, 46.07) * mm, "end": v(17.6, -57.93) * mm});
            skLineSegment(sketch, "E4.17.0.1", {"start": v(17.4, 46.07) * mm, "end": v(17.4, -57.93) * mm});
            skLineSegment(sketch, "E4.17.0.2", {"start": v(19.6, -57.93) * mm, "end": v(19.6, 46.07) * mm});
            skLineSegment(sketch, "E4.17.0.3", {"start": v(19.4, -57.93) * mm, "end": v(19.4, 46.07) * mm});
            skLineSegment(sketch, "E4.17.0.4", {"start": v(19.4, 45.87) * mm, "end": v(21.4, 45.87) * mm});
            skLineSegment(sketch, "E4.17.0.5", {"start": v(17.4, 46.07) * mm, "end": v(17.6, 46.07) * mm});
            skLineSegment(sketch, "E4.17.0.6", {"start": v(19.4, 46.07) * mm, "end": v(21.4, 46.07) * mm});
            skLineSegment(sketch, "E4.17.0.7", {"start": v(21.4, 46.07) * mm, "end": v(21.4, 45.87) * mm});
            skLineSegment(sketch, "E4.17.0.8", {"start": v(17.4, -57.73) * mm, "end": v(19.4, -57.73) * mm});
            skLineSegment(sketch, "E4.17.0.9", {"start": v(17.4, -57.93) * mm, "end": v(19.4, -57.93) * mm});
            skLineSegment(sketch, "E4.17.0.10", {"start": v(17.4, -57.93) * mm, "end": v(17.6, -57.93) * mm});
            skLineSegment(sketch, "E4.17.0.11", {"start": v(17.4, -57.93) * mm, "end": v(17.4, -57.73) * mm});
            skLineSegment(sketch, "E4.17.0.12", {"start": v(19.4, -57.93) * mm, "end": v(19.4, -57.73) * mm});
            skLineSegment(sketch, "E4.17.0.13", {"start": v(19.4, -57.93) * mm, "end": v(19.6, -57.93) * mm});
            skLineSegment(sketch, "E4.17.0.14", {"start": v(19.4, 46.07) * mm, "end": v(19.6, 46.07) * mm});
            skLineSegment(sketch, "E4.17.0.15", {"start": v(19.4, 46.07) * mm, "end": v(19.4, 45.87) * mm});
            skLineSegment(sketch, "E4.direction1", {"start": v(-50.6, -57.93) * mm, "end": v(-46.6, -57.93) * mm, "construction": true});
            skLineSegment(sketch, "E5.0.18.0", {"start": v(21.6, 46.07) * mm, "end": v(21.6, -57.93) * mm});
            skLineSegment(sketch, "E5.3.18.0", {"start": v(21.4, 46.07) * mm, "end": v(21.4, -57.93) * mm});
            skLineSegment(sketch, "E5.6.18.0", {"start": v(23.6, -57.93) * mm, "end": v(23.6, 46.07) * mm});
            skLineSegment(sketch, "E5.9.18.0", {"start": v(23.4, -57.93) * mm, "end": v(23.4, 46.07) * mm});
            skLineSegment(sketch, "E5.12.18.0", {"start": v(23.4, 45.87) * mm, "end": v(25.4, 45.87) * mm});
            skLineSegment(sketch, "E5.15.18.0", {"start": v(21.4, 46.07) * mm, "end": v(21.6, 46.07) * mm});
            skLineSegment(sketch, "E5.18.18.0", {"start": v(23.4, 46.07) * mm, "end": v(25.4, 46.07) * mm});
            skLineSegment(sketch, "E5.21.18.0", {"start": v(25.4, 46.07) * mm, "end": v(25.4, 45.87) * mm});
            skLineSegment(sketch, "E5.24.18.0", {"start": v(21.4, -57.73) * mm, "end": v(23.4, -57.73) * mm});
            skLineSegment(sketch, "E5.27.18.0", {"start": v(21.4, -57.93) * mm, "end": v(23.4, -57.93) * mm});
            skLineSegment(sketch, "E5.30.18.0", {"start": v(21.4, -57.93) * mm, "end": v(21.6, -57.93) * mm});
            skLineSegment(sketch, "E5.33.18.0", {"start": v(21.4, -57.93) * mm, "end": v(21.4, -57.73) * mm});
            skLineSegment(sketch, "E5.36.18.0", {"start": v(23.4, -57.93) * mm, "end": v(23.4, -57.73) * mm});
            skLineSegment(sketch, "E5.39.18.0", {"start": v(23.4, -57.93) * mm, "end": v(23.6, -57.93) * mm});
            skLineSegment(sketch, "E5.42.18.0", {"start": v(23.4, 46.07) * mm, "end": v(23.6, 46.07) * mm});
            skLineSegment(sketch, "E5.45.18.0", {"start": v(23.4, 46.07) * mm, "end": v(23.4, 45.87) * mm});
            skLineSegment(sketch, "E5.0.19.0", {"start": v(25.6, 46.07) * mm, "end": v(25.6, -57.93) * mm});
            skLineSegment(sketch, "E5.3.19.0", {"start": v(25.4, 46.07) * mm, "end": v(25.4, -57.93) * mm});
            skLineSegment(sketch, "E5.6.19.0", {"start": v(27.6, -57.93) * mm, "end": v(27.6, 46.07) * mm});
            skLineSegment(sketch, "E5.9.19.0", {"start": v(27.4, -57.93) * mm, "end": v(27.4, 46.07) * mm});
            skLineSegment(sketch, "E5.12.19.0", {"start": v(27.4, 45.87) * mm, "end": v(29.4, 45.87) * mm});
            skLineSegment(sketch, "E5.15.19.0", {"start": v(25.4, 46.07) * mm, "end": v(25.6, 46.07) * mm});
            skLineSegment(sketch, "E5.18.19.0", {"start": v(27.4, 46.07) * mm, "end": v(29.4, 46.07) * mm});
            skLineSegment(sketch, "E5.21.19.0", {"start": v(29.4, 46.07) * mm, "end": v(29.4, 45.87) * mm});
            skLineSegment(sketch, "E5.24.19.0", {"start": v(25.4, -57.73) * mm, "end": v(27.4, -57.73) * mm});
            skLineSegment(sketch, "E5.27.19.0", {"start": v(25.4, -57.93) * mm, "end": v(27.4, -57.93) * mm});
            skLineSegment(sketch, "E5.30.19.0", {"start": v(25.4, -57.93) * mm, "end": v(25.6, -57.93) * mm});
            skLineSegment(sketch, "E5.33.19.0", {"start": v(25.4, -57.93) * mm, "end": v(25.4, -57.73) * mm});
            skLineSegment(sketch, "E5.36.19.0", {"start": v(27.4, -57.93) * mm, "end": v(27.4, -57.73) * mm});
            skLineSegment(sketch, "E5.39.19.0", {"start": v(27.4, -57.93) * mm, "end": v(27.6, -57.93) * mm});
            skLineSegment(sketch, "E5.42.19.0", {"start": v(27.4, 46.07) * mm, "end": v(27.6, 46.07) * mm});
            skLineSegment(sketch, "E5.45.19.0", {"start": v(27.4, 46.07) * mm, "end": v(27.4, 45.87) * mm});
            skLineSegment(sketch, "E5.0.20.0", {"start": v(29.6, 46.07) * mm, "end": v(29.6, -57.93) * mm});
            skLineSegment(sketch, "E5.3.20.0", {"start": v(29.4, 46.07) * mm, "end": v(29.4, -57.93) * mm});
            skLineSegment(sketch, "E5.6.20.0", {"start": v(31.6, -57.93) * mm, "end": v(31.6, 46.07) * mm});
            skLineSegment(sketch, "E5.9.20.0", {"start": v(31.4, -57.93) * mm, "end": v(31.4, 46.07) * mm});
            skLineSegment(sketch, "E5.12.20.0", {"start": v(31.4, 45.87) * mm, "end": v(33.4, 45.87) * mm});
            skLineSegment(sketch, "E5.15.20.0", {"start": v(29.4, 46.07) * mm, "end": v(29.6, 46.07) * mm});
            skLineSegment(sketch, "E5.18.20.0", {"start": v(31.4, 46.07) * mm, "end": v(33.4, 46.07) * mm});
            skLineSegment(sketch, "E5.21.20.0", {"start": v(33.4, 46.07) * mm, "end": v(33.4, 45.87) * mm});
            skLineSegment(sketch, "E5.24.20.0", {"start": v(29.4, -57.73) * mm, "end": v(31.4, -57.73) * mm});
            skLineSegment(sketch, "E5.27.20.0", {"start": v(29.4, -57.93) * mm, "end": v(31.4, -57.93) * mm});
            skLineSegment(sketch, "E5.30.20.0", {"start": v(29.4, -57.93) * mm, "end": v(29.6, -57.93) * mm});
            skLineSegment(sketch, "E5.33.20.0", {"start": v(29.4, -57.93) * mm, "end": v(29.4, -57.73) * mm});
            skLineSegment(sketch, "E5.36.20.0", {"start": v(31.4, -57.93) * mm, "end": v(31.4, -57.73) * mm});
            skLineSegment(sketch, "E5.39.20.0", {"start": v(31.4, -57.93) * mm, "end": v(31.6, -57.93) * mm});
            skLineSegment(sketch, "E5.42.20.0", {"start": v(31.4, 46.07) * mm, "end": v(31.6, 46.07) * mm});
            skLineSegment(sketch, "E5.45.20.0", {"start": v(31.4, 46.07) * mm, "end": v(31.4, 45.87) * mm});
            skLineSegment(sketch, "E5.0.21.0", {"start": v(33.6, 46.07) * mm, "end": v(33.6, -57.93) * mm});
            skLineSegment(sketch, "E5.3.21.0", {"start": v(33.4, 46.07) * mm, "end": v(33.4, -57.93) * mm});
            skLineSegment(sketch, "E5.6.21.0", {"start": v(35.6, -57.93) * mm, "end": v(35.6, 46.07) * mm});
            skLineSegment(sketch, "E5.9.21.0", {"start": v(35.4, -57.93) * mm, "end": v(35.4, 46.07) * mm});
            skLineSegment(sketch, "E5.12.21.0", {"start": v(35.4, 45.87) * mm, "end": v(37.4, 45.87) * mm});
            skLineSegment(sketch, "E5.15.21.0", {"start": v(33.4, 46.07) * mm, "end": v(33.6, 46.07) * mm});
            skLineSegment(sketch, "E5.18.21.0", {"start": v(35.4, 46.07) * mm, "end": v(37.4, 46.07) * mm});
            skLineSegment(sketch, "E5.21.21.0", {"start": v(37.4, 46.07) * mm, "end": v(37.4, 45.87) * mm});
            skLineSegment(sketch, "E5.24.21.0", {"start": v(33.4, -57.73) * mm, "end": v(35.4, -57.73) * mm});
            skLineSegment(sketch, "E5.27.21.0", {"start": v(33.4, -57.93) * mm, "end": v(35.4, -57.93) * mm});
            skLineSegment(sketch, "E5.30.21.0", {"start": v(33.4, -57.93) * mm, "end": v(33.6, -57.93) * mm});
            skLineSegment(sketch, "E5.33.21.0", {"start": v(33.4, -57.93) * mm, "end": v(33.4, -57.73) * mm});
            skLineSegment(sketch, "E5.36.21.0", {"start": v(35.4, -57.93) * mm, "end": v(35.4, -57.73) * mm});
            skLineSegment(sketch, "E5.39.21.0", {"start": v(35.4, -57.93) * mm, "end": v(35.6, -57.93) * mm});
            skLineSegment(sketch, "E5.42.21.0", {"start": v(35.4, 46.07) * mm, "end": v(35.6, 46.07) * mm});
            skLineSegment(sketch, "E5.45.21.0", {"start": v(35.4, 46.07) * mm, "end": v(35.4, 45.87) * mm});
            skLineSegment(sketch, "E5.0.22.0", {"start": v(37.6, 46.07) * mm, "end": v(37.6, -57.93) * mm});
            skLineSegment(sketch, "E5.3.22.0", {"start": v(37.4, 46.07) * mm, "end": v(37.4, -57.93) * mm});
            skLineSegment(sketch, "E5.6.22.0", {"start": v(39.6, -57.93) * mm, "end": v(39.6, 46.07) * mm});
            skLineSegment(sketch, "E5.9.22.0", {"start": v(39.4, -57.93) * mm, "end": v(39.4, 46.07) * mm});
            skLineSegment(sketch, "E5.12.22.0", {"start": v(39.4, 45.87) * mm, "end": v(41.4, 45.87) * mm});
            skLineSegment(sketch, "E5.15.22.0", {"start": v(37.4, 46.07) * mm, "end": v(37.6, 46.07) * mm});
            skLineSegment(sketch, "E5.18.22.0", {"start": v(39.4, 46.07) * mm, "end": v(41.4, 46.07) * mm});
            skLineSegment(sketch, "E5.21.22.0", {"start": v(41.4, 46.07) * mm, "end": v(41.4, 45.87) * mm});
            skLineSegment(sketch, "E5.24.22.0", {"start": v(37.4, -57.73) * mm, "end": v(39.4, -57.73) * mm});
            skLineSegment(sketch, "E5.27.22.0", {"start": v(37.4, -57.93) * mm, "end": v(39.4, -57.93) * mm});
            skLineSegment(sketch, "E5.30.22.0", {"start": v(37.4, -57.93) * mm, "end": v(37.6, -57.93) * mm});
            skLineSegment(sketch, "E5.33.22.0", {"start": v(37.4, -57.93) * mm, "end": v(37.4, -57.73) * mm});
            skLineSegment(sketch, "E5.36.22.0", {"start": v(39.4, -57.93) * mm, "end": v(39.4, -57.73) * mm});
            skLineSegment(sketch, "E5.39.22.0", {"start": v(39.4, -57.93) * mm, "end": v(39.6, -57.93) * mm});
            skLineSegment(sketch, "E5.42.22.0", {"start": v(39.4, 46.07) * mm, "end": v(39.6, 46.07) * mm});
            skLineSegment(sketch, "E5.45.22.0", {"start": v(39.4, 46.07) * mm, "end": v(39.4, 45.87) * mm});
            skLineSegment(sketch, "E5.0.23.0", {"start": v(41.6, 46.07) * mm, "end": v(41.6, -57.93) * mm});
            skLineSegment(sketch, "E5.3.23.0", {"start": v(41.4, 46.07) * mm, "end": v(41.4, -57.93) * mm});
            skLineSegment(sketch, "E5.6.23.0", {"start": v(43.6, -57.93) * mm, "end": v(43.6, 46.07) * mm});
            skLineSegment(sketch, "E5.9.23.0", {"start": v(43.4, -57.93) * mm, "end": v(43.4, 46.07) * mm});
            skLineSegment(sketch, "E5.12.23.0", {"start": v(43.4, 45.87) * mm, "end": v(45.4, 45.87) * mm});
            skLineSegment(sketch, "E5.15.23.0", {"start": v(41.4, 46.07) * mm, "end": v(41.6, 46.07) * mm});
            skLineSegment(sketch, "E5.18.23.0", {"start": v(43.4, 46.07) * mm, "end": v(45.4, 46.07) * mm});
            skLineSegment(sketch, "E5.21.23.0", {"start": v(45.4, 46.07) * mm, "end": v(45.4, 45.87) * mm});
            skLineSegment(sketch, "E5.24.23.0", {"start": v(41.4, -57.73) * mm, "end": v(43.4, -57.73) * mm});
            skLineSegment(sketch, "E5.27.23.0", {"start": v(41.4, -57.93) * mm, "end": v(43.4, -57.93) * mm});
            skLineSegment(sketch, "E5.30.23.0", {"start": v(41.4, -57.93) * mm, "end": v(41.6, -57.93) * mm});
            skLineSegment(sketch, "E5.33.23.0", {"start": v(41.4, -57.93) * mm, "end": v(41.4, -57.73) * mm});
            skLineSegment(sketch, "E5.36.23.0", {"start": v(43.4, -57.93) * mm, "end": v(43.4, -57.73) * mm});
            skLineSegment(sketch, "E5.39.23.0", {"start": v(43.4, -57.93) * mm, "end": v(43.6, -57.93) * mm});
            skLineSegment(sketch, "E5.42.23.0", {"start": v(43.4, 46.07) * mm, "end": v(43.6, 46.07) * mm});
            skLineSegment(sketch, "E5.45.23.0", {"start": v(43.4, 46.07) * mm, "end": v(43.4, 45.87) * mm});
            skLineSegment(sketch, "E5.0.24.0", {"start": v(45.6, 46.07) * mm, "end": v(45.6, -57.93) * mm});
            skLineSegment(sketch, "E5.3.24.0", {"start": v(45.4, 46.07) * mm, "end": v(45.4, -57.93) * mm});
            skLineSegment(sketch, "E5.6.24.0", {"start": v(47.6, -57.93) * mm, "end": v(47.6, 46.07) * mm});
            skLineSegment(sketch, "E5.9.24.0", {"start": v(47.4, -57.93) * mm, "end": v(47.4, 46.07) * mm});
            skLineSegment(sketch, "E5.12.24.0", {"start": v(47.4, 45.87) * mm, "end": v(49.4, 45.87) * mm});
            skLineSegment(sketch, "E5.15.24.0", {"start": v(45.4, 46.07) * mm, "end": v(45.6, 46.07) * mm});
            skLineSegment(sketch, "E5.18.24.0", {"start": v(47.4, 46.07) * mm, "end": v(49.4, 46.07) * mm});
            skLineSegment(sketch, "E5.21.24.0", {"start": v(49.4, 46.07) * mm, "end": v(49.4, 45.87) * mm});
            skLineSegment(sketch, "E5.24.24.0", {"start": v(45.4, -57.73) * mm, "end": v(47.4, -57.73) * mm});
            skLineSegment(sketch, "E5.27.24.0", {"start": v(45.4, -57.93) * mm, "end": v(47.4, -57.93) * mm});
            skLineSegment(sketch, "E5.30.24.0", {"start": v(45.4, -57.93) * mm, "end": v(45.6, -57.93) * mm});
            skLineSegment(sketch, "E5.33.24.0", {"start": v(45.4, -57.93) * mm, "end": v(45.4, -57.73) * mm});
            skLineSegment(sketch, "E5.36.24.0", {"start": v(47.4, -57.93) * mm, "end": v(47.4, -57.73) * mm});
            skLineSegment(sketch, "E5.39.24.0", {"start": v(47.4, -57.93) * mm, "end": v(47.6, -57.93) * mm});
            skLineSegment(sketch, "E5.42.24.0", {"start": v(47.4, 46.07) * mm, "end": v(47.6, 46.07) * mm});
            skLineSegment(sketch, "E5.45.24.0", {"start": v(47.4, 46.07) * mm, "end": v(47.4, 45.87) * mm});
            skLineSegment(sketch, "E5.0.25.0", {"start": v(49.6, 46.07) * mm, "end": v(49.6, -57.93) * mm});
            skLineSegment(sketch, "E5.3.25.0", {"start": v(49.4, 46.07) * mm, "end": v(49.4, -57.93) * mm});
            skLineSegment(sketch, "E5.6.25.0", {"start": v(51.6, -57.93) * mm, "end": v(51.6, 46.07) * mm});
            skLineSegment(sketch, "E5.9.25.0", {"start": v(51.4, -57.93) * mm, "end": v(51.4, 46.07) * mm});
            skLineSegment(sketch, "E5.12.25.0", {"start": v(51.4, 45.87) * mm, "end": v(53.4, 45.87) * mm});
            skLineSegment(sketch, "E5.15.25.0", {"start": v(49.4, 46.07) * mm, "end": v(49.6, 46.07) * mm});
            skLineSegment(sketch, "E5.18.25.0", {"start": v(51.4, 46.07) * mm, "end": v(53.4, 46.07) * mm});
            skLineSegment(sketch, "E5.21.25.0", {"start": v(53.4, 46.07) * mm, "end": v(53.4, 45.87) * mm});
            skLineSegment(sketch, "E5.24.25.0", {"start": v(49.4, -57.73) * mm, "end": v(51.4, -57.73) * mm});
            skLineSegment(sketch, "E5.27.25.0", {"start": v(49.4, -57.93) * mm, "end": v(51.4, -57.93) * mm});
            skLineSegment(sketch, "E5.30.25.0", {"start": v(49.4, -57.93) * mm, "end": v(49.6, -57.93) * mm});
            skLineSegment(sketch, "E5.33.25.0", {"start": v(49.4, -57.93) * mm, "end": v(49.4, -57.73) * mm});
            skLineSegment(sketch, "E5.36.25.0", {"start": v(51.4, -57.93) * mm, "end": v(51.4, -57.73) * mm});
            skLineSegment(sketch, "E5.39.25.0", {"start": v(51.4, -57.93) * mm, "end": v(51.6, -57.93) * mm});
            skLineSegment(sketch, "E5.42.25.0", {"start": v(51.4, 46.07) * mm, "end": v(51.6, 46.07) * mm});
            skLineSegment(sketch, "E5.45.25.0", {"start": v(51.4, 46.07) * mm, "end": v(51.4, 45.87) * mm});
            skSolve(sketch);
        }
        {
            var Q0;
            {var subQ0=sQuery(id+"F0.wireOp",EDGE,"E5.18.25.0");var subQ1=sQuery(id+"F0.wireOp",EDGE,"E5.6.25.0");var subQ2=makeQuery(id+"F0.imprint","INTERSECT",VERTEX,{"derivedFrom":[subQ1,subQ0]});var subQ5=makeQuery(id+"F0.imprint","IMPRINT",EDGE,{"disambiguationData":[TD([[subQ2,1.0]])],"derivedFrom":subQ1});var subQ12=sQuery(id+"F0.wireOp",EDGE,"E5.39.25.0");var subQ13=sQuery(id+"F0.wireOp",EDGE,"E5.27.25.0");var subQ16=sQuery(id+"F0.wireOp",EDGE,"E5.0.25.0");var subQ17=makeQuery(id+"F0.imprint","INTERSECT",VERTEX,{"derivedFrom":[subQ16,subQ13]});var subQ19=makeQuery(id+"F0.imprint","IMPRINT",EDGE,{"disambiguationData":[TD([[subQ17,1.0]])],"derivedFrom":subQ16});var subQ25=sQuery(id+"F0.wireOp",EDGE,"E5.21.24.0");var subQ28=makeQuery(id+"F0.imprint","IMPRINT",EDGE,{"derivedFrom":subQ25});var subQ29=sQuery(id+"F0.wireOp",EDGE,"E5.18.24.0");var subQ30=sQuery(id+"F0.wireOp",EDGE,"E5.6.24.0");var subQ31=makeQuery(id+"F0.imprint","INTERSECT",VERTEX,{"derivedFrom":[subQ30,subQ29]});var subQ33=makeQuery(id+"F0.imprint","IMPRINT",EDGE,{"disambiguationData":[TD([[subQ31,1.0]])],"derivedFrom":subQ30});var subQ40=sQuery(id+"F0.wireOp",EDGE,"E5.39.24.0");var subQ41=sQuery(id+"F0.wireOp",EDGE,"E5.27.24.0");var subQ44=sQuery(id+"F0.wireOp",EDGE,"E5.0.24.0");var subQ45=makeQuery(id+"F0.imprint","INTERSECT",VERTEX,{"derivedFrom":[subQ44,subQ41]});var subQ47=makeQuery(id+"F0.imprint","IMPRINT",EDGE,{"disambiguationData":[TD([[subQ45,1.0]])],"derivedFrom":subQ44});var subQ53=sQuery(id+"F0.wireOp",EDGE,"E5.21.23.0");var subQ56=makeQuery(id+"F0.imprint","IMPRINT",EDGE,{"derivedFrom":subQ53});var subQ57=sQuery(id+"F0.wireOp",EDGE,"E5.18.23.0");var subQ58=sQuery(id+"F0.wireOp",EDGE,"E5.6.23.0");var subQ59=makeQuery(id+"F0.imprint","INTERSECT",VERTEX,{"derivedFrom":[subQ58,subQ57]});var subQ61=makeQuery(id+"F0.imprint","IMPRINT",EDGE,{"disambiguationData":[TD([[subQ59,1.0]])],"derivedFrom":subQ58});var subQ68=sQuery(id+"F0.wireOp",EDGE,"E5.39.23.0");var subQ69=sQuery(id+"F0.wireOp",EDGE,"E5.27.23.0");var subQ72=sQuery(id+"F0.wireOp",EDGE,"E5.0.23.0");var subQ73=makeQuery(id+"F0.imprint","INTERSECT",VERTEX,{"derivedFrom":[subQ72,subQ69]});var subQ75=makeQuery(id+"F0.imprint","IMPRINT",EDGE,{"disambiguationData":[TD([[subQ73,1.0]])],"derivedFrom":subQ72});var subQ81=sQuery(id+"F0.wireOp",EDGE,"E5.21.22.0");var subQ84=makeQuery(id+"F0.imprint","IMPRINT",EDGE,{"derivedFrom":subQ81});var subQ85=sQuery(id+"F0.wireOp",EDGE,"E5.18.22.0");var subQ86=sQuery(id+"F0.wireOp",EDGE,"E5.6.22.0");var subQ87=makeQuery(id+"F0.imprint","INTERSECT",VERTEX,{"derivedFrom":[subQ86,subQ85]});var subQ89=makeQuery(id+"F0.imprint","IMPRINT",EDGE,{"disambiguationData":[TD([[subQ87,1.0]])],"derivedFrom":subQ86});var subQ96=sQuery(id+"F0.wireOp",EDGE,"E5.39.22.0");var subQ97=sQuery(id+"F0.wireOp",EDGE,"E5.27.22.0");var subQ100=sQuery(id+"F0.wireOp",EDGE,"E5.0.22.0");var subQ101=makeQuery(id+"F0.imprint","INTERSECT",VERTEX,{"derivedFrom":[subQ100,subQ97]});var subQ103=makeQuery(id+"F0.imprint","IMPRINT",EDGE,{"disambiguationData":[TD([[subQ101,1.0]])],"derivedFrom":subQ100});var subQ109=sQuery(id+"F0.wireOp",EDGE,"E5.21.21.0");var subQ112=makeQuery(id+"F0.imprint","IMPRINT",EDGE,{"derivedFrom":subQ109});var subQ113=sQuery(id+"F0.wireOp",EDGE,"E5.18.21.0");var subQ114=sQuery(id+"F0.wireOp",EDGE,"E5.6.21.0");var subQ115=makeQuery(id+"F0.imprint","INTERSECT",VERTEX,{"derivedFrom":[subQ114,subQ113]});var subQ117=makeQuery(id+"F0.imprint","IMPRINT",EDGE,{"disambiguationData":[TD([[subQ115,1.0]])],"derivedFrom":subQ114});var subQ124=sQuery(id+"F0.wireOp",EDGE,"E5.39.21.0");var subQ125=sQuery(id+"F0.wireOp",EDGE,"E5.27.21.0");var subQ128=sQuery(id+"F0.wireOp",EDGE,"E5.0.21.0");var subQ129=makeQuery(id+"F0.imprint","INTERSECT",VERTEX,{"derivedFrom":[subQ128,subQ125]});var subQ131=makeQuery(id+"F0.imprint","IMPRINT",EDGE,{"disambiguationData":[TD([[subQ129,1.0]])],"derivedFrom":subQ128});var subQ137=sQuery(id+"F0.wireOp",EDGE,"E5.21.20.0");var subQ140=makeQuery(id+"F0.imprint","IMPRINT",EDGE,{"derivedFrom":subQ137});var subQ141=sQuery(id+"F0.wireOp",EDGE,"E5.18.20.0");var subQ142=sQuery(id+"F0.wireOp",EDGE,"E5.6.20.0");var subQ143=makeQuery(id+"F0.imprint","INTERSECT",VERTEX,{"derivedFrom":[subQ142,subQ141]});var subQ145=makeQuery(id+"F0.imprint","IMPRINT",EDGE,{"disambiguationData":[TD([[subQ143,1.0]])],"derivedFrom":subQ142});var subQ152=sQuery(id+"F0.wireOp",EDGE,"E5.39.20.0");var subQ153=sQuery(id+"F0.wireOp",EDGE,"E5.27.20.0");var subQ156=sQuery(id+"F0.wireOp",EDGE,"E5.0.20.0");var subQ157=makeQuery(id+"F0.imprint","INTERSECT",VERTEX,{"derivedFrom":[subQ156,subQ153]});var subQ159=makeQuery(id+"F0.imprint","IMPRINT",EDGE,{"disambiguationData":[TD([[subQ157,1.0]])],"derivedFrom":subQ156});var subQ165=sQuery(id+"F0.wireOp",EDGE,"E5.21.19.0");var subQ168=makeQuery(id+"F0.imprint","IMPRINT",EDGE,{"derivedFrom":subQ165});var subQ169=sQuery(id+"F0.wireOp",EDGE,"E5.18.19.0");var subQ170=sQuery(id+"F0.wireOp",EDGE,"E5.6.19.0");var subQ171=makeQuery(id+"F0.imprint","INTERSECT",VERTEX,{"derivedFrom":[subQ170,subQ169]});var subQ173=makeQuery(id+"F0.imprint","IMPRINT",EDGE,{"disambiguationData":[TD([[subQ171,1.0]])],"derivedFrom":subQ170});var subQ180=sQuery(id+"F0.wireOp",EDGE,"E5.39.19.0");var subQ181=sQuery(id+"F0.wireOp",EDGE,"E5.27.19.0");var subQ184=sQuery(id+"F0.wireOp",EDGE,"E5.0.19.0");var subQ185=makeQuery(id+"F0.imprint","INTERSECT",VERTEX,{"derivedFrom":[subQ184,subQ181]});var subQ187=makeQuery(id+"F0.imprint","IMPRINT",EDGE,{"disambiguationData":[TD([[subQ185,1.0]])],"derivedFrom":subQ184});var subQ193=sQuery(id+"F0.wireOp",EDGE,"E5.21.18.0");var subQ196=makeQuery(id+"F0.imprint","IMPRINT",EDGE,{"derivedFrom":subQ193});var subQ197=sQuery(id+"F0.wireOp",EDGE,"E5.18.18.0");var subQ198=sQuery(id+"F0.wireOp",EDGE,"E5.6.18.0");var subQ199=makeQuery(id+"F0.imprint","INTERSECT",VERTEX,{"derivedFrom":[subQ198,subQ197]});var subQ201=makeQuery(id+"F0.imprint","IMPRINT",EDGE,{"disambiguationData":[TD([[subQ199,1.0]])],"derivedFrom":subQ198});var subQ208=sQuery(id+"F0.wireOp",EDGE,"E5.39.18.0");var subQ209=sQuery(id+"F0.wireOp",EDGE,"E5.27.18.0");var subQ212=sQuery(id+"F0.wireOp",EDGE,"E5.0.18.0");var subQ213=makeQuery(id+"F0.imprint","INTERSECT",VERTEX,{"derivedFrom":[subQ212,subQ209]});var subQ215=makeQuery(id+"F0.imprint","IMPRINT",EDGE,{"disambiguationData":[TD([[subQ213,1.0]])],"derivedFrom":subQ212});var subQ221=sQuery(id+"F0.wireOp",EDGE,"E4.17.0.7");var subQ224=makeQuery(id+"F0.imprint","IMPRINT",EDGE,{"derivedFrom":subQ221});var subQ225=sQuery(id+"F0.wireOp",EDGE,"E4.17.0.6");var subQ226=sQuery(id+"F0.wireOp",EDGE,"E4.17.0.2");var subQ227=makeQuery(id+"F0.imprint","INTERSECT",VERTEX,{"derivedFrom":[subQ226,subQ225]});var subQ229=makeQuery(id+"F0.imprint","IMPRINT",EDGE,{"disambiguationData":[TD([[subQ227,1.0]])],"derivedFrom":subQ226});var subQ236=sQuery(id+"F0.wireOp",EDGE,"E4.17.0.13");var subQ237=sQuery(id+"F0.wireOp",EDGE,"E4.17.0.9");var subQ240=sQuery(id+"F0.wireOp",EDGE,"E4.17.0.0");var subQ241=makeQuery(id+"F0.imprint","INTERSECT",VERTEX,{"derivedFrom":[subQ240,subQ237]});var subQ243=makeQuery(id+"F0.imprint","IMPRINT",EDGE,{"disambiguationData":[TD([[subQ241,1.0]])],"derivedFrom":subQ240});var subQ249=sQuery(id+"F0.wireOp",EDGE,"E4.16.0.7");var subQ252=makeQuery(id+"F0.imprint","IMPRINT",EDGE,{"derivedFrom":subQ249});var subQ253=sQuery(id+"F0.wireOp",EDGE,"E4.16.0.6");var subQ254=sQuery(id+"F0.wireOp",EDGE,"E4.16.0.2");var subQ255=makeQuery(id+"F0.imprint","INTERSECT",VERTEX,{"derivedFrom":[subQ254,subQ253]});var subQ257=makeQuery(id+"F0.imprint","IMPRINT",EDGE,{"disambiguationData":[TD([[subQ255,1.0]])],"derivedFrom":subQ254});var subQ264=sQuery(id+"F0.wireOp",EDGE,"E4.16.0.13");var subQ265=sQuery(id+"F0.wireOp",EDGE,"E4.16.0.9");var subQ268=sQuery(id+"F0.wireOp",EDGE,"E4.16.0.0");var subQ269=makeQuery(id+"F0.imprint","INTERSECT",VERTEX,{"derivedFrom":[subQ268,subQ265]});var subQ271=makeQuery(id+"F0.imprint","IMPRINT",EDGE,{"disambiguationData":[TD([[subQ269,1.0]])],"derivedFrom":subQ268});var subQ277=sQuery(id+"F0.wireOp",EDGE,"E4.15.0.7");var subQ280=makeQuery(id+"F0.imprint","IMPRINT",EDGE,{"derivedFrom":subQ277});var subQ281=sQuery(id+"F0.wireOp",EDGE,"E4.15.0.6");var subQ282=sQuery(id+"F0.wireOp",EDGE,"E4.15.0.2");var subQ283=makeQuery(id+"F0.imprint","INTERSECT",VERTEX,{"derivedFrom":[subQ282,subQ281]});var subQ285=makeQuery(id+"F0.imprint","IMPRINT",EDGE,{"disambiguationData":[TD([[subQ283,1.0]])],"derivedFrom":subQ282});var subQ292=sQuery(id+"F0.wireOp",EDGE,"E4.15.0.13");var subQ293=sQuery(id+"F0.wireOp",EDGE,"E4.15.0.9");var subQ296=sQuery(id+"F0.wireOp",EDGE,"E4.15.0.0");var subQ297=makeQuery(id+"F0.imprint","INTERSECT",VERTEX,{"derivedFrom":[subQ296,subQ293]});var subQ299=makeQuery(id+"F0.imprint","IMPRINT",EDGE,{"disambiguationData":[TD([[subQ297,1.0]])],"derivedFrom":subQ296});var subQ305=sQuery(id+"F0.wireOp",EDGE,"E4.14.0.7");var subQ308=makeQuery(id+"F0.imprint","IMPRINT",EDGE,{"derivedFrom":subQ305});var subQ309=sQuery(id+"F0.wireOp",EDGE,"E4.14.0.6");var subQ310=sQuery(id+"F0.wireOp",EDGE,"E4.14.0.2");var subQ311=makeQuery(id+"F0.imprint","INTERSECT",VERTEX,{"derivedFrom":[subQ310,subQ309]});var subQ313=makeQuery(id+"F0.imprint","IMPRINT",EDGE,{"disambiguationData":[TD([[subQ311,1.0]])],"derivedFrom":subQ310});var subQ320=sQuery(id+"F0.wireOp",EDGE,"E4.14.0.13");var subQ321=sQuery(id+"F0.wireOp",EDGE,"E4.14.0.9");var subQ324=sQuery(id+"F0.wireOp",EDGE,"E4.14.0.0");var subQ325=makeQuery(id+"F0.imprint","INTERSECT",VERTEX,{"derivedFrom":[subQ324,subQ321]});var subQ327=makeQuery(id+"F0.imprint","IMPRINT",EDGE,{"disambiguationData":[TD([[subQ325,1.0]])],"derivedFrom":subQ324});var subQ333=sQuery(id+"F0.wireOp",EDGE,"E4.13.0.7");var subQ336=makeQuery(id+"F0.imprint","IMPRINT",EDGE,{"derivedFrom":subQ333});var subQ337=sQuery(id+"F0.wireOp",EDGE,"E4.13.0.6");var subQ338=sQuery(id+"F0.wireOp",EDGE,"E4.13.0.2");var subQ339=makeQuery(id+"F0.imprint","INTERSECT",VERTEX,{"derivedFrom":[subQ338,subQ337]});var subQ341=makeQuery(id+"F0.imprint","IMPRINT",EDGE,{"disambiguationData":[TD([[subQ339,1.0]])],"derivedFrom":subQ338});var subQ348=sQuery(id+"F0.wireOp",EDGE,"E4.13.0.13");var subQ349=sQuery(id+"F0.wireOp",EDGE,"E4.13.0.9");var subQ352=sQuery(id+"F0.wireOp",EDGE,"E4.13.0.0");var subQ353=makeQuery(id+"F0.imprint","INTERSECT",VERTEX,{"derivedFrom":[subQ352,subQ349]});var subQ355=makeQuery(id+"F0.imprint","IMPRINT",EDGE,{"disambiguationData":[TD([[subQ353,1.0]])],"derivedFrom":subQ352});var subQ361=sQuery(id+"F0.wireOp",EDGE,"E4.12.0.7");var subQ364=makeQuery(id+"F0.imprint","IMPRINT",EDGE,{"derivedFrom":subQ361});var subQ365=sQuery(id+"F0.wireOp",EDGE,"E4.12.0.6");var subQ366=sQuery(id+"F0.wireOp",EDGE,"E4.12.0.2");var subQ367=makeQuery(id+"F0.imprint","INTERSECT",VERTEX,{"derivedFrom":[subQ366,subQ365]});var subQ369=makeQuery(id+"F0.imprint","IMPRINT",EDGE,{"disambiguationData":[TD([[subQ367,1.0]])],"derivedFrom":subQ366});var subQ376=sQuery(id+"F0.wireOp",EDGE,"E4.12.0.13");var subQ377=sQuery(id+"F0.wireOp",EDGE,"E4.12.0.9");var subQ380=sQuery(id+"F0.wireOp",EDGE,"E4.12.0.0");var subQ381=makeQuery(id+"F0.imprint","INTERSECT",VERTEX,{"derivedFrom":[subQ380,subQ377]});var subQ383=makeQuery(id+"F0.imprint","IMPRINT",EDGE,{"disambiguationData":[TD([[subQ381,1.0]])],"derivedFrom":subQ380});var subQ389=sQuery(id+"F0.wireOp",EDGE,"E4.11.0.7");var subQ392=makeQuery(id+"F0.imprint","IMPRINT",EDGE,{"derivedFrom":subQ389});var subQ393=sQuery(id+"F0.wireOp",EDGE,"E4.11.0.6");var subQ394=sQuery(id+"F0.wireOp",EDGE,"E4.11.0.2");var subQ395=makeQuery(id+"F0.imprint","INTERSECT",VERTEX,{"derivedFrom":[subQ394,subQ393]});var subQ397=makeQuery(id+"F0.imprint","IMPRINT",EDGE,{"disambiguationData":[TD([[subQ395,1.0]])],"derivedFrom":subQ394});var subQ404=sQuery(id+"F0.wireOp",EDGE,"E4.11.0.13");var subQ405=sQuery(id+"F0.wireOp",EDGE,"E4.11.0.9");var subQ408=sQuery(id+"F0.wireOp",EDGE,"E4.11.0.0");var subQ409=makeQuery(id+"F0.imprint","INTERSECT",VERTEX,{"derivedFrom":[subQ408,subQ405]});var subQ411=makeQuery(id+"F0.imprint","IMPRINT",EDGE,{"disambiguationData":[TD([[subQ409,1.0]])],"derivedFrom":subQ408});var subQ417=sQuery(id+"F0.wireOp",EDGE,"E4.10.0.7");var subQ420=makeQuery(id+"F0.imprint","IMPRINT",EDGE,{"derivedFrom":subQ417});var subQ421=sQuery(id+"F0.wireOp",EDGE,"E4.10.0.6");var subQ422=sQuery(id+"F0.wireOp",EDGE,"E4.10.0.2");var subQ423=makeQuery(id+"F0.imprint","INTERSECT",VERTEX,{"derivedFrom":[subQ422,subQ421]});var subQ425=makeQuery(id+"F0.imprint","IMPRINT",EDGE,{"disambiguationData":[TD([[subQ423,1.0]])],"derivedFrom":subQ422});var subQ432=sQuery(id+"F0.wireOp",EDGE,"E4.10.0.13");var subQ433=sQuery(id+"F0.wireOp",EDGE,"E4.10.0.9");var subQ436=sQuery(id+"F0.wireOp",EDGE,"E4.10.0.0");var subQ437=makeQuery(id+"F0.imprint","INTERSECT",VERTEX,{"derivedFrom":[subQ436,subQ433]});var subQ439=makeQuery(id+"F0.imprint","IMPRINT",EDGE,{"disambiguationData":[TD([[subQ437,1.0]])],"derivedFrom":subQ436});var subQ445=sQuery(id+"F0.wireOp",EDGE,"E4.9.0.7");var subQ448=makeQuery(id+"F0.imprint","IMPRINT",EDGE,{"derivedFrom":subQ445});var subQ449=sQuery(id+"F0.wireOp",EDGE,"E4.9.0.6");var subQ450=sQuery(id+"F0.wireOp",EDGE,"E4.9.0.2");var subQ451=makeQuery(id+"F0.imprint","INTERSECT",VERTEX,{"derivedFrom":[subQ450,subQ449]});var subQ453=makeQuery(id+"F0.imprint","IMPRINT",EDGE,{"disambiguationData":[TD([[subQ451,1.0]])],"derivedFrom":subQ450});var subQ460=sQuery(id+"F0.wireOp",EDGE,"E4.9.0.13");var subQ461=sQuery(id+"F0.wireOp",EDGE,"E4.9.0.9");var subQ464=sQuery(id+"F0.wireOp",EDGE,"E4.9.0.0");var subQ465=makeQuery(id+"F0.imprint","INTERSECT",VERTEX,{"derivedFrom":[subQ464,subQ461]});var subQ467=makeQuery(id+"F0.imprint","IMPRINT",EDGE,{"disambiguationData":[TD([[subQ465,1.0]])],"derivedFrom":subQ464});var subQ473=sQuery(id+"F0.wireOp",EDGE,"E4.8.0.7");var subQ476=makeQuery(id+"F0.imprint","IMPRINT",EDGE,{"derivedFrom":subQ473});var subQ477=sQuery(id+"F0.wireOp",EDGE,"E4.8.0.6");var subQ478=sQuery(id+"F0.wireOp",EDGE,"E4.8.0.2");var subQ479=makeQuery(id+"F0.imprint","INTERSECT",VERTEX,{"derivedFrom":[subQ478,subQ477]});var subQ481=makeQuery(id+"F0.imprint","IMPRINT",EDGE,{"disambiguationData":[TD([[subQ479,1.0]])],"derivedFrom":subQ478});var subQ488=sQuery(id+"F0.wireOp",EDGE,"E4.8.0.13");var subQ489=sQuery(id+"F0.wireOp",EDGE,"E4.8.0.9");var subQ492=sQuery(id+"F0.wireOp",EDGE,"E4.8.0.0");var subQ493=makeQuery(id+"F0.imprint","INTERSECT",VERTEX,{"derivedFrom":[subQ492,subQ489]});var subQ495=makeQuery(id+"F0.imprint","IMPRINT",EDGE,{"disambiguationData":[TD([[subQ493,1.0]])],"derivedFrom":subQ492});var subQ501=sQuery(id+"F0.wireOp",EDGE,"E4.7.0.7");var subQ504=makeQuery(id+"F0.imprint","IMPRINT",EDGE,{"derivedFrom":subQ501});var subQ505=sQuery(id+"F0.wireOp",EDGE,"E4.7.0.6");var subQ506=sQuery(id+"F0.wireOp",EDGE,"E4.7.0.2");var subQ507=makeQuery(id+"F0.imprint","INTERSECT",VERTEX,{"derivedFrom":[subQ506,subQ505]});var subQ509=makeQuery(id+"F0.imprint","IMPRINT",EDGE,{"disambiguationData":[TD([[subQ507,1.0]])],"derivedFrom":subQ506});var subQ516=sQuery(id+"F0.wireOp",EDGE,"E4.7.0.13");var subQ517=sQuery(id+"F0.wireOp",EDGE,"E4.7.0.9");var subQ520=sQuery(id+"F0.wireOp",EDGE,"E4.7.0.0");var subQ521=makeQuery(id+"F0.imprint","INTERSECT",VERTEX,{"derivedFrom":[subQ520,subQ517]});var subQ523=makeQuery(id+"F0.imprint","IMPRINT",EDGE,{"disambiguationData":[TD([[subQ521,1.0]])],"derivedFrom":subQ520});var subQ529=sQuery(id+"F0.wireOp",EDGE,"E4.6.0.7");var subQ532=makeQuery(id+"F0.imprint","IMPRINT",EDGE,{"derivedFrom":subQ529});var subQ533=sQuery(id+"F0.wireOp",EDGE,"E4.6.0.6");var subQ534=sQuery(id+"F0.wireOp",EDGE,"E4.6.0.2");var subQ535=makeQuery(id+"F0.imprint","INTERSECT",VERTEX,{"derivedFrom":[subQ534,subQ533]});var subQ537=makeQuery(id+"F0.imprint","IMPRINT",EDGE,{"disambiguationData":[TD([[subQ535,1.0]])],"derivedFrom":subQ534});var subQ544=sQuery(id+"F0.wireOp",EDGE,"E4.6.0.13");var subQ545=sQuery(id+"F0.wireOp",EDGE,"E4.6.0.9");var subQ548=sQuery(id+"F0.wireOp",EDGE,"E4.6.0.0");var subQ549=makeQuery(id+"F0.imprint","INTERSECT",VERTEX,{"derivedFrom":[subQ548,subQ545]});var subQ551=makeQuery(id+"F0.imprint","IMPRINT",EDGE,{"disambiguationData":[TD([[subQ549,1.0]])],"derivedFrom":subQ548});var subQ557=sQuery(id+"F0.wireOp",EDGE,"E4.5.0.7");var subQ560=makeQuery(id+"F0.imprint","IMPRINT",EDGE,{"derivedFrom":subQ557});var subQ561=sQuery(id+"F0.wireOp",EDGE,"E4.5.0.6");var subQ562=sQuery(id+"F0.wireOp",EDGE,"E4.5.0.2");var subQ563=makeQuery(id+"F0.imprint","INTERSECT",VERTEX,{"derivedFrom":[subQ562,subQ561]});var subQ565=makeQuery(id+"F0.imprint","IMPRINT",EDGE,{"disambiguationData":[TD([[subQ563,1.0]])],"derivedFrom":subQ562});var subQ572=sQuery(id+"F0.wireOp",EDGE,"E4.5.0.13");var subQ573=sQuery(id+"F0.wireOp",EDGE,"E4.5.0.9");var subQ576=sQuery(id+"F0.wireOp",EDGE,"E4.5.0.0");var subQ577=makeQuery(id+"F0.imprint","INTERSECT",VERTEX,{"derivedFrom":[subQ576,subQ573]});var subQ579=makeQuery(id+"F0.imprint","IMPRINT",EDGE,{"disambiguationData":[TD([[subQ577,1.0]])],"derivedFrom":subQ576});var subQ585=sQuery(id+"F0.wireOp",EDGE,"E4.4.0.7");var subQ588=makeQuery(id+"F0.imprint","IMPRINT",EDGE,{"derivedFrom":subQ585});var subQ589=sQuery(id+"F0.wireOp",EDGE,"E4.4.0.6");var subQ590=sQuery(id+"F0.wireOp",EDGE,"E4.4.0.2");var subQ591=makeQuery(id+"F0.imprint","INTERSECT",VERTEX,{"derivedFrom":[subQ590,subQ589]});var subQ593=makeQuery(id+"F0.imprint","IMPRINT",EDGE,{"disambiguationData":[TD([[subQ591,1.0]])],"derivedFrom":subQ590});var subQ600=sQuery(id+"F0.wireOp",EDGE,"E4.4.0.13");var subQ601=sQuery(id+"F0.wireOp",EDGE,"E4.4.0.9");var subQ604=sQuery(id+"F0.wireOp",EDGE,"E4.4.0.0");var subQ605=makeQuery(id+"F0.imprint","INTERSECT",VERTEX,{"derivedFrom":[subQ604,subQ601]});var subQ607=makeQuery(id+"F0.imprint","IMPRINT",EDGE,{"disambiguationData":[TD([[subQ605,1.0]])],"derivedFrom":subQ604});var subQ613=sQuery(id+"F0.wireOp",EDGE,"E4.3.0.7");var subQ616=makeQuery(id+"F0.imprint","IMPRINT",EDGE,{"derivedFrom":subQ613});var subQ617=sQuery(id+"F0.wireOp",EDGE,"E4.3.0.6");var subQ618=sQuery(id+"F0.wireOp",EDGE,"E4.3.0.2");var subQ619=makeQuery(id+"F0.imprint","INTERSECT",VERTEX,{"derivedFrom":[subQ618,subQ617]});var subQ621=makeQuery(id+"F0.imprint","IMPRINT",EDGE,{"disambiguationData":[TD([[subQ619,1.0]])],"derivedFrom":subQ618});var subQ628=sQuery(id+"F0.wireOp",EDGE,"E4.3.0.13");var subQ629=sQuery(id+"F0.wireOp",EDGE,"E4.3.0.9");var subQ632=sQuery(id+"F0.wireOp",EDGE,"E4.3.0.0");var subQ633=makeQuery(id+"F0.imprint","INTERSECT",VERTEX,{"derivedFrom":[subQ632,subQ629]});var subQ635=makeQuery(id+"F0.imprint","IMPRINT",EDGE,{"disambiguationData":[TD([[subQ633,1.0]])],"derivedFrom":subQ632});var subQ641=sQuery(id+"F0.wireOp",EDGE,"E4.2.0.7");var subQ644=makeQuery(id+"F0.imprint","IMPRINT",EDGE,{"derivedFrom":subQ641});var subQ645=sQuery(id+"F0.wireOp",EDGE,"E4.2.0.6");var subQ646=sQuery(id+"F0.wireOp",EDGE,"E4.2.0.2");var subQ647=makeQuery(id+"F0.imprint","INTERSECT",VERTEX,{"derivedFrom":[subQ646,subQ645]});var subQ649=makeQuery(id+"F0.imprint","IMPRINT",EDGE,{"disambiguationData":[TD([[subQ647,1.0]])],"derivedFrom":subQ646});var subQ656=sQuery(id+"F0.wireOp",EDGE,"E4.2.0.13");var subQ657=sQuery(id+"F0.wireOp",EDGE,"E4.2.0.9");var subQ660=sQuery(id+"F0.wireOp",EDGE,"E4.2.0.0");var subQ661=makeQuery(id+"F0.imprint","INTERSECT",VERTEX,{"derivedFrom":[subQ660,subQ657]});var subQ663=makeQuery(id+"F0.imprint","IMPRINT",EDGE,{"disambiguationData":[TD([[subQ661,1.0]])],"derivedFrom":subQ660});var subQ669=sQuery(id+"F0.wireOp",EDGE,"E4.1.0.7");var subQ672=makeQuery(id+"F0.imprint","IMPRINT",EDGE,{"derivedFrom":subQ669});var subQ673=sQuery(id+"F0.wireOp",EDGE,"E4.1.0.6");var subQ674=sQuery(id+"F0.wireOp",EDGE,"E4.1.0.2");var subQ675=makeQuery(id+"F0.imprint","INTERSECT",VERTEX,{"derivedFrom":[subQ674,subQ673]});var subQ677=makeQuery(id+"F0.imprint","IMPRINT",EDGE,{"disambiguationData":[TD([[subQ675,1.0]])],"derivedFrom":subQ674});var subQ684=sQuery(id+"F0.wireOp",EDGE,"E4.1.0.13");var subQ685=sQuery(id+"F0.wireOp",EDGE,"E4.1.0.9");var subQ688=sQuery(id+"F0.wireOp",EDGE,"E4.1.0.0");var subQ689=makeQuery(id+"F0.imprint","INTERSECT",VERTEX,{"derivedFrom":[subQ688,subQ685]});var subQ691=makeQuery(id+"F0.imprint","IMPRINT",EDGE,{"disambiguationData":[TD([[subQ689,1.0]])],"derivedFrom":subQ688});var subQ697=sQuery(id+"F0.wireOp",EDGE,"E3.right");var subQ700=makeQuery(id+"F0.imprint","IMPRINT",EDGE,{"derivedFrom":subQ697});var subQ701=sQuery(id+"F0.wireOp",EDGE,"E3.bottom");var subQ703=sQuery(id+"F0.wireOp",EDGE,"E2.top");var subQ709=sQuery(id+"F0.wireOp",EDGE,"E1.right");var subQ713=makeQuery(id+"F0.imprint","IMPRINT",EDGE,{"derivedFrom":subQ709});var subQ714=sQuery(id+"F0.wireOp",EDGE,"E1.bottom");var subQ716=sQuery(id+"F0.wireOp",EDGE,"E0.top");var subQ722=sQuery(id+"F0.wireOp",EDGE,"E5.21.25.0");var subQ723=sQuery(id+"F0.wireOp",EDGE,"E0.bottom");Q0=qUnion([makeQuery(id+"F0.imprint","IMPRINT",FACE,{"disambiguationData":[TD([[makeQuery(id+"F0.imprint","IMPRINT",EDGE,{"derivedFrom":subQ723}),-1.0]])]}),makeQuery(id+"F0.imprint","IMPRINT",FACE,{"disambiguationData":[TD([[makeQuery(id+"F0.imprint","IMPRINT",EDGE,{"derivedFrom":subQ722}),-1.0]])]}),makeQuery(id+"F0.imprint","IMPRINT",FACE,{"disambiguationData":[TD([[makeQuery(id+"F0.imprint","IMPRINT",EDGE,{"derivedFrom":subQ716}),1.0]])]}),makeQuery(id+"F0.imprint","IMPRINT",FACE,{"disambiguationData":[TD([[makeQuery(id+"F0.imprint","IMPRINT",EDGE,{"derivedFrom":subQ714}),1.0]])]}),makeQuery(id+"F0.imprint","IMPRINT",FACE,{"disambiguationData":[TD([[subQ713,-1.0]])]}),makeQuery(id+"F0.imprint","IMPRINT",FACE,{"disambiguationData":[TD([[makeQuery(id+"F0.imprint","IMPRINT",EDGE,{"derivedFrom":subQ703}),-1.0]])]}),makeQuery(id+"F0.imprint","IMPRINT",FACE,{"disambiguationData":[TD([[makeQuery(id+"F0.imprint","IMPRINT",EDGE,{"derivedFrom":subQ701}),-1.0]])]}),makeQuery(id+"F0.imprint","IMPRINT",FACE,{"disambiguationData":[TD([[subQ700,1.0]])]}),makeQuery(id+"F0.imprint","IMPRINT",FACE,{"disambiguationData":[TD([[subQ691,-1.0]])]}),makeQuery(id+"F0.imprint","IMPRINT",FACE,{"disambiguationData":[TD([[subQ691,1.0]])]}),makeQuery(id+"F0.imprint","IMPRINT",FACE,{"disambiguationData":[TD([[makeQuery(id+"F0.imprint","IMPRINT",EDGE,{"derivedFrom":subQ684}),1.0]])]}),makeQuery(id+"F0.imprint","IMPRINT",FACE,{"disambiguationData":[TD([[subQ677,1.0]])]}),makeQuery(id+"F0.imprint","IMPRINT",FACE,{"disambiguationData":[TD([[subQ672,-1.0]])]}),makeQuery(id+"F0.imprint","IMPRINT",FACE,{"disambiguationData":[TD([[subQ672,1.0]])]}),makeQuery(id+"F0.imprint","IMPRINT",FACE,{"disambiguationData":[TD([[subQ663,-1.0]])]}),makeQuery(id+"F0.imprint","IMPRINT",FACE,{"disambiguationData":[TD([[subQ663,1.0]])]}),makeQuery(id+"F0.imprint","IMPRINT",FACE,{"disambiguationData":[TD([[makeQuery(id+"F0.imprint","IMPRINT",EDGE,{"derivedFrom":subQ656}),1.0]])]}),makeQuery(id+"F0.imprint","IMPRINT",FACE,{"disambiguationData":[TD([[subQ649,1.0]])]}),makeQuery(id+"F0.imprint","IMPRINT",FACE,{"disambiguationData":[TD([[subQ644,-1.0]])]}),makeQuery(id+"F0.imprint","IMPRINT",FACE,{"disambiguationData":[TD([[subQ644,1.0]])]}),makeQuery(id+"F0.imprint","IMPRINT",FACE,{"disambiguationData":[TD([[subQ635,-1.0]])]}),makeQuery(id+"F0.imprint","IMPRINT",FACE,{"disambiguationData":[TD([[subQ635,1.0]])]}),makeQuery(id+"F0.imprint","IMPRINT",FACE,{"disambiguationData":[TD([[makeQuery(id+"F0.imprint","IMPRINT",EDGE,{"derivedFrom":subQ628}),1.0]])]}),makeQuery(id+"F0.imprint","IMPRINT",FACE,{"disambiguationData":[TD([[subQ621,1.0]])]}),makeQuery(id+"F0.imprint","IMPRINT",FACE,{"disambiguationData":[TD([[subQ616,-1.0]])]}),makeQuery(id+"F0.imprint","IMPRINT",FACE,{"disambiguationData":[TD([[subQ616,1.0]])]}),makeQuery(id+"F0.imprint","IMPRINT",FACE,{"disambiguationData":[TD([[subQ607,-1.0]])]}),makeQuery(id+"F0.imprint","IMPRINT",FACE,{"disambiguationData":[TD([[subQ607,1.0]])]}),makeQuery(id+"F0.imprint","IMPRINT",FACE,{"disambiguationData":[TD([[makeQuery(id+"F0.imprint","IMPRINT",EDGE,{"derivedFrom":subQ600}),1.0]])]}),makeQuery(id+"F0.imprint","IMPRINT",FACE,{"disambiguationData":[TD([[subQ593,1.0]])]}),makeQuery(id+"F0.imprint","IMPRINT",FACE,{"disambiguationData":[TD([[subQ588,-1.0]])]}),makeQuery(id+"F0.imprint","IMPRINT",FACE,{"disambiguationData":[TD([[subQ588,1.0]])]}),makeQuery(id+"F0.imprint","IMPRINT",FACE,{"disambiguationData":[TD([[subQ579,-1.0]])]}),makeQuery(id+"F0.imprint","IMPRINT",FACE,{"disambiguationData":[TD([[subQ579,1.0]])]}),makeQuery(id+"F0.imprint","IMPRINT",FACE,{"disambiguationData":[TD([[makeQuery(id+"F0.imprint","IMPRINT",EDGE,{"derivedFrom":subQ572}),1.0]])]}),makeQuery(id+"F0.imprint","IMPRINT",FACE,{"disambiguationData":[TD([[subQ565,1.0]])]}),makeQuery(id+"F0.imprint","IMPRINT",FACE,{"disambiguationData":[TD([[subQ560,-1.0]])]}),makeQuery(id+"F0.imprint","IMPRINT",FACE,{"disambiguationData":[TD([[subQ560,1.0]])]}),makeQuery(id+"F0.imprint","IMPRINT",FACE,{"disambiguationData":[TD([[subQ551,-1.0]])]}),makeQuery(id+"F0.imprint","IMPRINT",FACE,{"disambiguationData":[TD([[subQ551,1.0]])]}),makeQuery(id+"F0.imprint","IMPRINT",FACE,{"disambiguationData":[TD([[makeQuery(id+"F0.imprint","IMPRINT",EDGE,{"derivedFrom":subQ544}),1.0]])]}),makeQuery(id+"F0.imprint","IMPRINT",FACE,{"disambiguationData":[TD([[subQ537,1.0]])]}),makeQuery(id+"F0.imprint","IMPRINT",FACE,{"disambiguationData":[TD([[subQ532,-1.0]])]}),makeQuery(id+"F0.imprint","IMPRINT",FACE,{"disambiguationData":[TD([[subQ532,1.0]])]}),makeQuery(id+"F0.imprint","IMPRINT",FACE,{"disambiguationData":[TD([[subQ523,-1.0]])]}),makeQuery(id+"F0.imprint","IMPRINT",FACE,{"disambiguationData":[TD([[subQ523,1.0]])]}),makeQuery(id+"F0.imprint","IMPRINT",FACE,{"disambiguationData":[TD([[makeQuery(id+"F0.imprint","IMPRINT",EDGE,{"derivedFrom":subQ516}),1.0]])]}),makeQuery(id+"F0.imprint","IMPRINT",FACE,{"disambiguationData":[TD([[subQ509,1.0]])]}),makeQuery(id+"F0.imprint","IMPRINT",FACE,{"disambiguationData":[TD([[subQ504,-1.0]])]}),makeQuery(id+"F0.imprint","IMPRINT",FACE,{"disambiguationData":[TD([[subQ504,1.0]])]}),makeQuery(id+"F0.imprint","IMPRINT",FACE,{"disambiguationData":[TD([[subQ495,-1.0]])]}),makeQuery(id+"F0.imprint","IMPRINT",FACE,{"disambiguationData":[TD([[subQ495,1.0]])]}),makeQuery(id+"F0.imprint","IMPRINT",FACE,{"disambiguationData":[TD([[makeQuery(id+"F0.imprint","IMPRINT",EDGE,{"derivedFrom":subQ488}),1.0]])]}),makeQuery(id+"F0.imprint","IMPRINT",FACE,{"disambiguationData":[TD([[subQ481,1.0]])]}),makeQuery(id+"F0.imprint","IMPRINT",FACE,{"disambiguationData":[TD([[subQ476,-1.0]])]}),makeQuery(id+"F0.imprint","IMPRINT",FACE,{"disambiguationData":[TD([[subQ476,1.0]])]}),makeQuery(id+"F0.imprint","IMPRINT",FACE,{"disambiguationData":[TD([[subQ467,-1.0]])]}),makeQuery(id+"F0.imprint","IMPRINT",FACE,{"disambiguationData":[TD([[subQ467,1.0]])]}),makeQuery(id+"F0.imprint","IMPRINT",FACE,{"disambiguationData":[TD([[makeQuery(id+"F0.imprint","IMPRINT",EDGE,{"derivedFrom":subQ460}),1.0]])]}),makeQuery(id+"F0.imprint","IMPRINT",FACE,{"disambiguationData":[TD([[subQ453,1.0]])]}),makeQuery(id+"F0.imprint","IMPRINT",FACE,{"disambiguationData":[TD([[subQ448,-1.0]])]}),makeQuery(id+"F0.imprint","IMPRINT",FACE,{"disambiguationData":[TD([[subQ448,1.0]])]}),makeQuery(id+"F0.imprint","IMPRINT",FACE,{"disambiguationData":[TD([[subQ439,-1.0]])]}),makeQuery(id+"F0.imprint","IMPRINT",FACE,{"disambiguationData":[TD([[subQ439,1.0]])]}),makeQuery(id+"F0.imprint","IMPRINT",FACE,{"disambiguationData":[TD([[makeQuery(id+"F0.imprint","IMPRINT",EDGE,{"derivedFrom":subQ432}),1.0]])]}),makeQuery(id+"F0.imprint","IMPRINT",FACE,{"disambiguationData":[TD([[subQ425,1.0]])]}),makeQuery(id+"F0.imprint","IMPRINT",FACE,{"disambiguationData":[TD([[subQ420,-1.0]])]}),makeQuery(id+"F0.imprint","IMPRINT",FACE,{"disambiguationData":[TD([[subQ420,1.0]])]}),makeQuery(id+"F0.imprint","IMPRINT",FACE,{"disambiguationData":[TD([[subQ411,-1.0]])]}),makeQuery(id+"F0.imprint","IMPRINT",FACE,{"disambiguationData":[TD([[subQ411,1.0]])]}),makeQuery(id+"F0.imprint","IMPRINT",FACE,{"disambiguationData":[TD([[makeQuery(id+"F0.imprint","IMPRINT",EDGE,{"derivedFrom":subQ404}),1.0]])]}),makeQuery(id+"F0.imprint","IMPRINT",FACE,{"disambiguationData":[TD([[subQ397,1.0]])]}),makeQuery(id+"F0.imprint","IMPRINT",FACE,{"disambiguationData":[TD([[subQ392,-1.0]])]}),makeQuery(id+"F0.imprint","IMPRINT",FACE,{"disambiguationData":[TD([[subQ392,1.0]])]}),makeQuery(id+"F0.imprint","IMPRINT",FACE,{"disambiguationData":[TD([[subQ383,-1.0]])]}),makeQuery(id+"F0.imprint","IMPRINT",FACE,{"disambiguationData":[TD([[subQ383,1.0]])]}),makeQuery(id+"F0.imprint","IMPRINT",FACE,{"disambiguationData":[TD([[makeQuery(id+"F0.imprint","IMPRINT",EDGE,{"derivedFrom":subQ376}),1.0]])]}),makeQuery(id+"F0.imprint","IMPRINT",FACE,{"disambiguationData":[TD([[subQ369,1.0]])]}),makeQuery(id+"F0.imprint","IMPRINT",FACE,{"disambiguationData":[TD([[subQ364,-1.0]])]}),makeQuery(id+"F0.imprint","IMPRINT",FACE,{"disambiguationData":[TD([[subQ364,1.0]])]}),makeQuery(id+"F0.imprint","IMPRINT",FACE,{"disambiguationData":[TD([[subQ355,-1.0]])]}),makeQuery(id+"F0.imprint","IMPRINT",FACE,{"disambiguationData":[TD([[subQ355,1.0]])]}),makeQuery(id+"F0.imprint","IMPRINT",FACE,{"disambiguationData":[TD([[makeQuery(id+"F0.imprint","IMPRINT",EDGE,{"derivedFrom":subQ348}),1.0]])]}),makeQuery(id+"F0.imprint","IMPRINT",FACE,{"disambiguationData":[TD([[subQ341,1.0]])]}),makeQuery(id+"F0.imprint","IMPRINT",FACE,{"disambiguationData":[TD([[subQ336,-1.0]])]}),makeQuery(id+"F0.imprint","IMPRINT",FACE,{"disambiguationData":[TD([[subQ336,1.0]])]}),makeQuery(id+"F0.imprint","IMPRINT",FACE,{"disambiguationData":[TD([[subQ327,-1.0]])]}),makeQuery(id+"F0.imprint","IMPRINT",FACE,{"disambiguationData":[TD([[subQ327,1.0]])]}),makeQuery(id+"F0.imprint","IMPRINT",FACE,{"disambiguationData":[TD([[makeQuery(id+"F0.imprint","IMPRINT",EDGE,{"derivedFrom":subQ320}),1.0]])]}),makeQuery(id+"F0.imprint","IMPRINT",FACE,{"disambiguationData":[TD([[subQ313,1.0]])]}),makeQuery(id+"F0.imprint","IMPRINT",FACE,{"disambiguationData":[TD([[subQ308,-1.0]])]}),makeQuery(id+"F0.imprint","IMPRINT",FACE,{"disambiguationData":[TD([[subQ308,1.0]])]}),makeQuery(id+"F0.imprint","IMPRINT",FACE,{"disambiguationData":[TD([[subQ299,-1.0]])]}),makeQuery(id+"F0.imprint","IMPRINT",FACE,{"disambiguationData":[TD([[subQ299,1.0]])]}),makeQuery(id+"F0.imprint","IMPRINT",FACE,{"disambiguationData":[TD([[makeQuery(id+"F0.imprint","IMPRINT",EDGE,{"derivedFrom":subQ292}),1.0]])]}),makeQuery(id+"F0.imprint","IMPRINT",FACE,{"disambiguationData":[TD([[subQ285,1.0]])]}),makeQuery(id+"F0.imprint","IMPRINT",FACE,{"disambiguationData":[TD([[subQ280,-1.0]])]}),makeQuery(id+"F0.imprint","IMPRINT",FACE,{"disambiguationData":[TD([[subQ280,1.0]])]}),makeQuery(id+"F0.imprint","IMPRINT",FACE,{"disambiguationData":[TD([[subQ271,-1.0]])]}),makeQuery(id+"F0.imprint","IMPRINT",FACE,{"disambiguationData":[TD([[subQ271,1.0]])]}),makeQuery(id+"F0.imprint","IMPRINT",FACE,{"disambiguationData":[TD([[makeQuery(id+"F0.imprint","IMPRINT",EDGE,{"derivedFrom":subQ264}),1.0]])]}),makeQuery(id+"F0.imprint","IMPRINT",FACE,{"disambiguationData":[TD([[subQ257,1.0]])]}),makeQuery(id+"F0.imprint","IMPRINT",FACE,{"disambiguationData":[TD([[subQ252,-1.0]])]}),makeQuery(id+"F0.imprint","IMPRINT",FACE,{"disambiguationData":[TD([[subQ252,1.0]])]}),makeQuery(id+"F0.imprint","IMPRINT",FACE,{"disambiguationData":[TD([[subQ243,-1.0]])]}),makeQuery(id+"F0.imprint","IMPRINT",FACE,{"disambiguationData":[TD([[subQ243,1.0]])]}),makeQuery(id+"F0.imprint","IMPRINT",FACE,{"disambiguationData":[TD([[makeQuery(id+"F0.imprint","IMPRINT",EDGE,{"derivedFrom":subQ236}),1.0]])]}),makeQuery(id+"F0.imprint","IMPRINT",FACE,{"disambiguationData":[TD([[subQ229,1.0]])]}),makeQuery(id+"F0.imprint","IMPRINT",FACE,{"disambiguationData":[TD([[subQ224,-1.0]])]}),makeQuery(id+"F0.imprint","IMPRINT",FACE,{"disambiguationData":[TD([[subQ224,1.0]])]}),makeQuery(id+"F0.imprint","IMPRINT",FACE,{"disambiguationData":[TD([[subQ215,-1.0]])]}),makeQuery(id+"F0.imprint","IMPRINT",FACE,{"disambiguationData":[TD([[subQ215,1.0]])]}),makeQuery(id+"F0.imprint","IMPRINT",FACE,{"disambiguationData":[TD([[makeQuery(id+"F0.imprint","IMPRINT",EDGE,{"derivedFrom":subQ208}),1.0]])]}),makeQuery(id+"F0.imprint","IMPRINT",FACE,{"disambiguationData":[TD([[subQ201,1.0]])]}),makeQuery(id+"F0.imprint","IMPRINT",FACE,{"disambiguationData":[TD([[subQ196,-1.0]])]}),makeQuery(id+"F0.imprint","IMPRINT",FACE,{"disambiguationData":[TD([[subQ196,1.0]])]}),makeQuery(id+"F0.imprint","IMPRINT",FACE,{"disambiguationData":[TD([[subQ187,-1.0]])]}),makeQuery(id+"F0.imprint","IMPRINT",FACE,{"disambiguationData":[TD([[subQ187,1.0]])]}),makeQuery(id+"F0.imprint","IMPRINT",FACE,{"disambiguationData":[TD([[makeQuery(id+"F0.imprint","IMPRINT",EDGE,{"derivedFrom":subQ180}),1.0]])]}),makeQuery(id+"F0.imprint","IMPRINT",FACE,{"disambiguationData":[TD([[subQ173,1.0]])]}),makeQuery(id+"F0.imprint","IMPRINT",FACE,{"disambiguationData":[TD([[subQ168,-1.0]])]}),makeQuery(id+"F0.imprint","IMPRINT",FACE,{"disambiguationData":[TD([[subQ168,1.0]])]}),makeQuery(id+"F0.imprint","IMPRINT",FACE,{"disambiguationData":[TD([[subQ159,-1.0]])]}),makeQuery(id+"F0.imprint","IMPRINT",FACE,{"disambiguationData":[TD([[subQ159,1.0]])]}),makeQuery(id+"F0.imprint","IMPRINT",FACE,{"disambiguationData":[TD([[makeQuery(id+"F0.imprint","IMPRINT",EDGE,{"derivedFrom":subQ152}),1.0]])]}),makeQuery(id+"F0.imprint","IMPRINT",FACE,{"disambiguationData":[TD([[subQ145,1.0]])]}),makeQuery(id+"F0.imprint","IMPRINT",FACE,{"disambiguationData":[TD([[subQ140,-1.0]])]}),makeQuery(id+"F0.imprint","IMPRINT",FACE,{"disambiguationData":[TD([[subQ140,1.0]])]}),makeQuery(id+"F0.imprint","IMPRINT",FACE,{"disambiguationData":[TD([[subQ131,-1.0]])]}),makeQuery(id+"F0.imprint","IMPRINT",FACE,{"disambiguationData":[TD([[subQ131,1.0]])]}),makeQuery(id+"F0.imprint","IMPRINT",FACE,{"disambiguationData":[TD([[makeQuery(id+"F0.imprint","IMPRINT",EDGE,{"derivedFrom":subQ124}),1.0]])]}),makeQuery(id+"F0.imprint","IMPRINT",FACE,{"disambiguationData":[TD([[subQ117,1.0]])]}),makeQuery(id+"F0.imprint","IMPRINT",FACE,{"disambiguationData":[TD([[subQ112,-1.0]])]}),makeQuery(id+"F0.imprint","IMPRINT",FACE,{"disambiguationData":[TD([[subQ112,1.0]])]}),makeQuery(id+"F0.imprint","IMPRINT",FACE,{"disambiguationData":[TD([[subQ103,-1.0]])]}),makeQuery(id+"F0.imprint","IMPRINT",FACE,{"disambiguationData":[TD([[subQ103,1.0]])]}),makeQuery(id+"F0.imprint","IMPRINT",FACE,{"disambiguationData":[TD([[makeQuery(id+"F0.imprint","IMPRINT",EDGE,{"derivedFrom":subQ96}),1.0]])]}),makeQuery(id+"F0.imprint","IMPRINT",FACE,{"disambiguationData":[TD([[subQ89,1.0]])]}),makeQuery(id+"F0.imprint","IMPRINT",FACE,{"disambiguationData":[TD([[subQ84,-1.0]])]}),makeQuery(id+"F0.imprint","IMPRINT",FACE,{"disambiguationData":[TD([[subQ84,1.0]])]}),makeQuery(id+"F0.imprint","IMPRINT",FACE,{"disambiguationData":[TD([[subQ75,-1.0]])]}),makeQuery(id+"F0.imprint","IMPRINT",FACE,{"disambiguationData":[TD([[subQ75,1.0]])]}),makeQuery(id+"F0.imprint","IMPRINT",FACE,{"disambiguationData":[TD([[makeQuery(id+"F0.imprint","IMPRINT",EDGE,{"derivedFrom":subQ68}),1.0]])]}),makeQuery(id+"F0.imprint","IMPRINT",FACE,{"disambiguationData":[TD([[subQ61,1.0]])]}),makeQuery(id+"F0.imprint","IMPRINT",FACE,{"disambiguationData":[TD([[subQ56,-1.0]])]}),makeQuery(id+"F0.imprint","IMPRINT",FACE,{"disambiguationData":[TD([[subQ56,1.0]])]}),makeQuery(id+"F0.imprint","IMPRINT",FACE,{"disambiguationData":[TD([[subQ47,-1.0]])]}),makeQuery(id+"F0.imprint","IMPRINT",FACE,{"disambiguationData":[TD([[subQ47,1.0]])]}),makeQuery(id+"F0.imprint","IMPRINT",FACE,{"disambiguationData":[TD([[makeQuery(id+"F0.imprint","IMPRINT",EDGE,{"derivedFrom":subQ40}),1.0]])]}),makeQuery(id+"F0.imprint","IMPRINT",FACE,{"disambiguationData":[TD([[subQ33,1.0]])]}),makeQuery(id+"F0.imprint","IMPRINT",FACE,{"disambiguationData":[TD([[subQ28,-1.0]])]}),makeQuery(id+"F0.imprint","IMPRINT",FACE,{"disambiguationData":[TD([[subQ28,1.0]])]}),makeQuery(id+"F0.imprint","IMPRINT",FACE,{"disambiguationData":[TD([[subQ19,-1.0]])]}),makeQuery(id+"F0.imprint","IMPRINT",FACE,{"disambiguationData":[TD([[subQ19,1.0]])]}),makeQuery(id+"F0.imprint","IMPRINT",FACE,{"disambiguationData":[TD([[makeQuery(id+"F0.imprint","IMPRINT",EDGE,{"derivedFrom":subQ12}),1.0]])]}),makeQuery(id+"F0.imprint","IMPRINT",FACE,{"disambiguationData":[TD([[subQ5,1.0]])]})]);}
            extrude(context, id + "F1", {"entities" : qUnion([Q0]), "depth" : 0.4 * mm, "offsetDistance" : 25 * mm});
        }
    });
